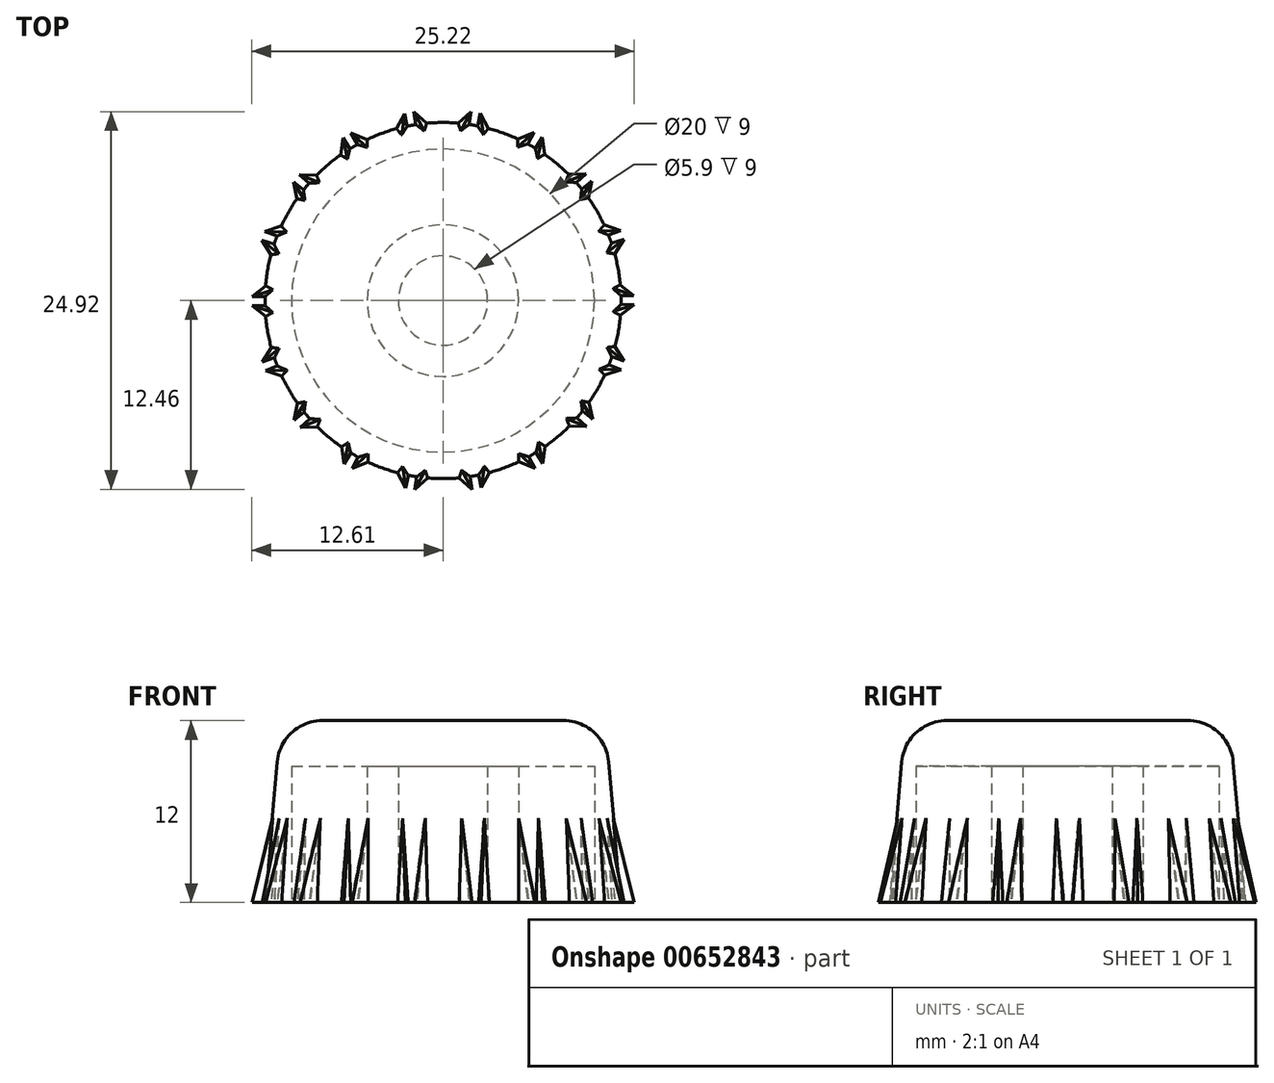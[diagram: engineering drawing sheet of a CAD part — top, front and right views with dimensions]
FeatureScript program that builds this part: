
annotation { "Feature Type Name" : "Feature", "Feature Type Description" : "" }
export const myFeature = defineFeature(function(context is Context, id is Id, definition is map)
    precondition{}
    {
        {
            var Q0;
            Q0=qCreatedBy(makeId("Top.planeOp"),FACE);
            var sketch = newSketch(context, id + "F0", { "sketchPlane" : qUnion([Q0])});
            skLineSegment(sketch, "E0", {"start": v(0, 0) * mm, "end": v(1.85, 12.46) * mm});
            skLineSegment(sketch, "E1", {"start": v(-1.92, 12.46) * mm, "end": v(0, 0) * mm});
            skLineSegment(sketch, "E2", {"start": v(-1.92, 12.46) * mm, "end": v(-0.04, 10.77) * mm});
            skPoint(sketch, "E2.endSnap0", {"position": v(-0.04, 12.46) * mm});
            skLineSegment(sketch, "E3", {"start": v(-0.04, 10.77) * mm, "end": v(1.85, 12.46) * mm});
            skLineSegment(sketch, "E4.1.0", {"start": v(-6.07, 11.05) * mm, "end": v(0, 0) * mm});
            skLineSegment(sketch, "E4.1.1", {"start": v(-3.72, 10.1) * mm, "end": v(-2.53, 12.34) * mm});
            skLineSegment(sketch, "E4.1.2", {"start": v(-6.07, 11.05) * mm, "end": v(-3.72, 10.1) * mm});
            skPoint(sketch, "E4.1.3", {"position": v(-4.3, 11.7) * mm});
            skLineSegment(sketch, "E4.1.4", {"start": v(0, 0) * mm, "end": v(-2.53, 12.34) * mm});
            skLineSegment(sketch, "E4.2.0", {"start": v(-9.48, 8.31) * mm, "end": v(0, 0) * mm});
            skLineSegment(sketch, "E4.2.1", {"start": v(-6.95, 8.23) * mm, "end": v(-6.6, 10.74) * mm});
            skLineSegment(sketch, "E4.2.2", {"start": v(-9.48, 8.31) * mm, "end": v(-6.95, 8.23) * mm});
            skPoint(sketch, "E4.2.3", {"position": v(-8.04, 9.52) * mm});
            skLineSegment(sketch, "E4.2.4", {"start": v(0, 0) * mm, "end": v(-6.6, 10.74) * mm});
            skPoint(sketch, "E4.center", {"position": v(0, 0) * mm});
            skLineSegment(sketch, "E5.1.3.0", {"start": v(-11.75, 4.57) * mm, "end": v(0, 0) * mm});
            skLineSegment(sketch, "E5.3.3.0", {"start": v(-9.35, 5.35) * mm, "end": v(-9.87, 7.83) * mm});
            skLineSegment(sketch, "E5.6.3.0", {"start": v(-11.75, 4.57) * mm, "end": v(-9.35, 5.35) * mm});
            skPoint(sketch, "E5.9.3.0", {"position": v(-10.81, 6.2) * mm});
            skLineSegment(sketch, "E5.10.3.0", {"start": v(0, 0) * mm, "end": v(-9.87, 7.83) * mm});
            skLineSegment(sketch, "E5.1.4.0", {"start": v(-12.6, 0.27) * mm, "end": v(0, 0) * mm});
            skLineSegment(sketch, "E5.3.4.0", {"start": v(-10.61, 1.83) * mm, "end": v(-11.95, 3.98) * mm});
            skLineSegment(sketch, "E5.6.4.0", {"start": v(-12.6, 0.27) * mm, "end": v(-10.61, 1.83) * mm});
            skPoint(sketch, "E5.9.4.0", {"position": v(-12.28, 2.13) * mm});
            skLineSegment(sketch, "E5.10.4.0", {"start": v(0, 0) * mm, "end": v(-11.95, 3.98) * mm});
            skLineSegment(sketch, "E5.1.5.0", {"start": v(-11.94, -4.06) * mm, "end": v(0, 0) * mm});
            skLineSegment(sketch, "E5.3.5.0", {"start": v(-10.6, -1.9) * mm, "end": v(-12.6, -0.35) * mm});
            skLineSegment(sketch, "E5.6.5.0", {"start": v(-11.94, -4.06) * mm, "end": v(-10.6, -1.9) * mm});
            skPoint(sketch, "E5.9.5.0", {"position": v(-12.27, -2.2) * mm});
            skLineSegment(sketch, "E5.10.5.0", {"start": v(0, 0) * mm, "end": v(-12.6, -0.35) * mm});
            skLineSegment(sketch, "E5.1.6.0", {"start": v(-9.83, -7.9) * mm, "end": v(0, 0) * mm});
            skLineSegment(sketch, "E5.3.6.0", {"start": v(-9.3, -5.42) * mm, "end": v(-11.72, -4.63) * mm});
            skLineSegment(sketch, "E5.6.6.0", {"start": v(-9.83, -7.9) * mm, "end": v(-9.3, -5.42) * mm});
            skPoint(sketch, "E5.9.6.0", {"position": v(-10.78, -6.26) * mm});
            skLineSegment(sketch, "E5.10.6.0", {"start": v(0, 0) * mm, "end": v(-11.72, -4.63) * mm});
            skLineSegment(sketch, "E5.1.7.0", {"start": v(-6.54, -10.78) * mm, "end": v(0, 0) * mm});
            skLineSegment(sketch, "E5.3.7.0", {"start": v(-6.9, -8.28) * mm, "end": v(-9.43, -8.36) * mm});
            skLineSegment(sketch, "E5.6.7.0", {"start": v(-6.54, -10.78) * mm, "end": v(-6.9, -8.28) * mm});
            skPoint(sketch, "E5.9.7.0", {"position": v(-7.98, -9.57) * mm});
            skLineSegment(sketch, "E5.10.7.0", {"start": v(0, 0) * mm, "end": v(-9.43, -8.36) * mm});
            skLineSegment(sketch, "E6.1.8.0", {"start": v(-2.46, -12.37) * mm, "end": v(0, 0) * mm});
            skLineSegment(sketch, "E6.3.8.0", {"start": v(-3.65, -10.13) * mm, "end": v(-6, -11.08) * mm});
            skLineSegment(sketch, "E6.6.8.0", {"start": v(-2.46, -12.37) * mm, "end": v(-3.65, -10.13) * mm});
            skPoint(sketch, "E6.9.8.0", {"position": v(-4.23, -11.72) * mm});
            skLineSegment(sketch, "E6.10.8.0", {"start": v(0, 0) * mm, "end": v(-6, -11.08) * mm});
            skLineSegment(sketch, "E6.1.9.0", {"start": v(1.92, -12.46) * mm, "end": v(0, 0) * mm});
            skLineSegment(sketch, "E6.3.9.0", {"start": v(0.04, -10.77) * mm, "end": v(-1.85, -12.46) * mm});
            skLineSegment(sketch, "E6.6.9.0", {"start": v(1.92, -12.46) * mm, "end": v(0.04, -10.77) * mm});
            skPoint(sketch, "E6.9.9.0", {"position": v(0.04, -12.46) * mm});
            skLineSegment(sketch, "E6.10.9.0", {"start": v(0, 0) * mm, "end": v(-1.85, -12.46) * mm});
            skLineSegment(sketch, "E6.1.10.0", {"start": v(6.07, -11.05) * mm, "end": v(0, 0) * mm});
            skLineSegment(sketch, "E6.3.10.0", {"start": v(3.72, -10.1) * mm, "end": v(2.53, -12.34) * mm});
            skLineSegment(sketch, "E6.6.10.0", {"start": v(6.07, -11.05) * mm, "end": v(3.72, -10.1) * mm});
            skPoint(sketch, "E6.9.10.0", {"position": v(4.3, -11.7) * mm});
            skLineSegment(sketch, "E6.10.10.0", {"start": v(0, 0) * mm, "end": v(2.53, -12.34) * mm});
            skLineSegment(sketch, "E6.1.11.0", {"start": v(9.48, -8.31) * mm, "end": v(0, 0) * mm});
            skLineSegment(sketch, "E6.3.11.0", {"start": v(6.95, -8.23) * mm, "end": v(6.6, -10.74) * mm});
            skLineSegment(sketch, "E6.6.11.0", {"start": v(9.48, -8.31) * mm, "end": v(6.95, -8.23) * mm});
            skPoint(sketch, "E6.9.11.0", {"position": v(8.04, -9.52) * mm});
            skLineSegment(sketch, "E6.10.11.0", {"start": v(0, 0) * mm, "end": v(6.6, -10.74) * mm});
            skLineSegment(sketch, "E6.1.12.0", {"start": v(11.75, -4.57) * mm, "end": v(0, 0) * mm});
            skLineSegment(sketch, "E6.3.12.0", {"start": v(9.35, -5.35) * mm, "end": v(9.87, -7.83) * mm});
            skLineSegment(sketch, "E6.6.12.0", {"start": v(11.75, -4.57) * mm, "end": v(9.35, -5.35) * mm});
            skPoint(sketch, "E6.9.12.0", {"position": v(10.81, -6.2) * mm});
            skLineSegment(sketch, "E6.10.12.0", {"start": v(0, 0) * mm, "end": v(9.87, -7.83) * mm});
            skLineSegment(sketch, "E6.1.13.0", {"start": v(12.6, -0.27) * mm, "end": v(0, 0) * mm});
            skLineSegment(sketch, "E6.3.13.0", {"start": v(10.61, -1.83) * mm, "end": v(11.95, -3.98) * mm});
            skLineSegment(sketch, "E6.6.13.0", {"start": v(12.6, -0.27) * mm, "end": v(10.61, -1.83) * mm});
            skPoint(sketch, "E6.9.13.0", {"position": v(12.28, -2.13) * mm});
            skLineSegment(sketch, "E6.10.13.0", {"start": v(0, 0) * mm, "end": v(11.95, -3.98) * mm});
            skLineSegment(sketch, "E6.1.14.0", {"start": v(11.94, 4.06) * mm, "end": v(0, 0) * mm});
            skLineSegment(sketch, "E6.3.14.0", {"start": v(10.6, 1.9) * mm, "end": v(12.6, 0.35) * mm});
            skLineSegment(sketch, "E6.6.14.0", {"start": v(11.94, 4.06) * mm, "end": v(10.6, 1.9) * mm});
            skPoint(sketch, "E6.9.14.0", {"position": v(12.27, 2.2) * mm});
            skLineSegment(sketch, "E6.10.14.0", {"start": v(0, 0) * mm, "end": v(12.6, 0.35) * mm});
            skLineSegment(sketch, "E6.1.15.0", {"start": v(9.83, 7.9) * mm, "end": v(0, 0) * mm});
            skLineSegment(sketch, "E6.3.15.0", {"start": v(9.3, 5.42) * mm, "end": v(11.72, 4.63) * mm});
            skLineSegment(sketch, "E6.6.15.0", {"start": v(9.83, 7.9) * mm, "end": v(9.3, 5.42) * mm});
            skPoint(sketch, "E6.9.15.0", {"position": v(10.78, 6.26) * mm});
            skLineSegment(sketch, "E6.10.15.0", {"start": v(0, 0) * mm, "end": v(11.72, 4.63) * mm});
            skLineSegment(sketch, "E6.1.16.0", {"start": v(6.54, 10.78) * mm, "end": v(0, 0) * mm});
            skLineSegment(sketch, "E6.3.16.0", {"start": v(6.9, 8.28) * mm, "end": v(9.43, 8.36) * mm});
            skLineSegment(sketch, "E6.6.16.0", {"start": v(6.54, 10.78) * mm, "end": v(6.9, 8.28) * mm});
            skPoint(sketch, "E6.9.16.0", {"position": v(7.98, 9.57) * mm});
            skLineSegment(sketch, "E6.10.16.0", {"start": v(0, 0) * mm, "end": v(9.43, 8.36) * mm});
            skLineSegment(sketch, "E6.1.17.0", {"start": v(2.46, 12.37) * mm, "end": v(0, 0) * mm});
            skLineSegment(sketch, "E6.3.17.0", {"start": v(3.65, 10.13) * mm, "end": v(6, 11.08) * mm});
            skLineSegment(sketch, "E6.6.17.0", {"start": v(2.46, 12.37) * mm, "end": v(3.65, 10.13) * mm});
            skPoint(sketch, "E6.9.17.0", {"position": v(4.23, 11.72) * mm});
            skLineSegment(sketch, "E6.10.17.0", {"start": v(0, 0) * mm, "end": v(6, 11.08) * mm});
            skCircle(sketch, "E7", {"center": v(0, 0) * mm, "radius": 10.77 * mm});
            skCircle(sketch, "E8", {"center": v(0, 0) * mm, "radius": 11.75 * mm});
            skSolve(sketch);
        }
        {
            var Q0;
            {var subQ0=sQuery(id+"F0.wireOp",EDGE,"E5.10.6.0");var subQ3=sQuery(id+"F0.wireOp",EDGE,"E7");var subQ5=makeQuery(id+"F0.imprint","INTERSECT",VERTEX,{"derivedFrom":[subQ0,subQ3]});Q0=makeQuery(id+"F0.imprint","IMPRINT",FACE,{"disambiguationData":[TD([[makeQuery(id+"F0.imprint","IMPRINT",EDGE,{"disambiguationData":[TD([[subQ5,-1.0]])],"derivedFrom":subQ3}),1.0]])]});}
            var Q1;
            {var subQ1=sQuery(id+"F0.wireOp",EDGE,"E4.1.1");var subQ3=sQuery(id+"F0.wireOp",EDGE,"E8");var subQ4=makeQuery(id+"F0.imprint","INTERSECT",VERTEX,{"derivedFrom":[subQ1,subQ3]});Q1=makeQuery(id+"F0.imprint","IMPRINT",FACE,{"disambiguationData":[TD([[makeQuery(id+"F0.imprint","IMPRINT",EDGE,{"disambiguationData":[TD([[subQ4,-1.0]])],"derivedFrom":subQ3}),1.0]])]});}
            var Q2;
            {var subQ0=sQuery(id+"F0.wireOp",EDGE,"E8");var subQ1=sQuery(id+"F0.wireOp",EDGE,"E5.1.5.0");var subQ2=makeQuery(id+"F0.imprint","INTERSECT",VERTEX,{"derivedFrom":[subQ1,subQ0]});Q2=makeQuery(id+"F0.imprint","IMPRINT",FACE,{"disambiguationData":[TD([[makeQuery(id+"F0.imprint","IMPRINT",EDGE,{"disambiguationData":[TD([[subQ2,-1.0]])],"derivedFrom":subQ1}),-1.0]])]});}
            var Q3;
            {var subQ0=sQuery(id+"F0.wireOp",EDGE,"E6.10.12.0");var subQ3=sQuery(id+"F0.wireOp",EDGE,"E7");var subQ5=makeQuery(id+"F0.imprint","INTERSECT",VERTEX,{"derivedFrom":[subQ0,subQ3]});Q3=makeQuery(id+"F0.imprint","IMPRINT",FACE,{"disambiguationData":[TD([[makeQuery(id+"F0.imprint","IMPRINT",EDGE,{"disambiguationData":[TD([[subQ5,-1.0]])],"derivedFrom":subQ3}),1.0]])]});}
            var Q4;
            {var subQ3=sQuery(id+"F0.wireOp",EDGE,"E8");var subQ5=sQuery(id+"F0.wireOp",EDGE,"E6.10.17.0");var subQ6=makeQuery(id+"F0.imprint","INTERSECT",VERTEX,{"derivedFrom":[subQ5,subQ3]});Q4=makeQuery(id+"F0.imprint","IMPRINT",FACE,{"disambiguationData":[TD([[makeQuery(id+"F0.imprint","IMPRINT",EDGE,{"disambiguationData":[TD([[subQ6,1.0]])],"derivedFrom":subQ5}),1.0]])]});}
            var Q5;
            {var subQ1=sQuery(id+"F0.wireOp",EDGE,"E5.1.5.0");var subQ3=sQuery(id+"F0.wireOp",EDGE,"E7");var subQ4=makeQuery(id+"F0.imprint","INTERSECT",VERTEX,{"derivedFrom":[subQ1,subQ3]});Q5=makeQuery(id+"F0.imprint","IMPRINT",FACE,{"disambiguationData":[TD([[makeQuery(id+"F0.imprint","IMPRINT",EDGE,{"disambiguationData":[TD([[subQ4,-1.0]])],"derivedFrom":subQ3}),1.0]])]});}
            var Q6;
            {var subQ0=sQuery(id+"F0.wireOp",EDGE,"E8");var subQ1=sQuery(id+"F0.wireOp",EDGE,"E6.1.17.0");var subQ2=makeQuery(id+"F0.imprint","INTERSECT",VERTEX,{"derivedFrom":[subQ1,subQ0]});Q6=makeQuery(id+"F0.imprint","IMPRINT",FACE,{"disambiguationData":[TD([[makeQuery(id+"F0.imprint","IMPRINT",EDGE,{"disambiguationData":[TD([[subQ2,-1.0]])],"derivedFrom":subQ1}),1.0]])]});}
            var Q7;
            {var subQ1=sQuery(id+"F0.wireOp",EDGE,"E1");var subQ3=sQuery(id+"F0.wireOp",EDGE,"E7");var subQ4=makeQuery(id+"F0.imprint","INTERSECT",VERTEX,{"derivedFrom":[subQ1,subQ3]});Q7=makeQuery(id+"F0.imprint","IMPRINT",FACE,{"disambiguationData":[TD([[makeQuery(id+"F0.imprint","IMPRINT",EDGE,{"disambiguationData":[TD([[subQ4,-1.0]])],"derivedFrom":subQ3}),1.0]])]});}
            var Q8;
            {var subQ1=sQuery(id+"F0.wireOp",EDGE,"E0");var subQ3=sQuery(id+"F0.wireOp",EDGE,"E7");var subQ4=makeQuery(id+"F0.imprint","INTERSECT",VERTEX,{"derivedFrom":[subQ1,subQ3]});Q8=makeQuery(id+"F0.imprint","IMPRINT",FACE,{"disambiguationData":[TD([[makeQuery(id+"F0.imprint","IMPRINT",EDGE,{"disambiguationData":[TD([[subQ4,1.0]])],"derivedFrom":subQ3}),1.0]])]});}
            var Q9;
            {var subQ3=sQuery(id+"F0.wireOp",EDGE,"E8");var subQ5=sQuery(id+"F0.wireOp",EDGE,"E6.10.15.0");var subQ6=makeQuery(id+"F0.imprint","INTERSECT",VERTEX,{"derivedFrom":[subQ5,subQ3]});Q9=makeQuery(id+"F0.imprint","IMPRINT",FACE,{"disambiguationData":[TD([[makeQuery(id+"F0.imprint","IMPRINT",EDGE,{"disambiguationData":[TD([[subQ6,1.0]])],"derivedFrom":subQ5}),1.0]])]});}
            var Q10;
            {var subQ0=sQuery(id+"F0.wireOp",EDGE,"E4.2.4");var subQ1=sQuery(id+"F0.wireOp",EDGE,"E4.2.1");var subQ2=makeQuery(id+"F0.imprint","INTERSECT",VERTEX,{"derivedFrom":[subQ1,subQ0]});Q10=makeQuery(id+"F0.imprint","IMPRINT",FACE,{"disambiguationData":[TD([[makeQuery(id+"F0.imprint","IMPRINT",EDGE,{"disambiguationData":[TD([[subQ2,1.0]])],"derivedFrom":subQ1}),-1.0]])]});}
            var Q11;
            {var subQ0=sQuery(id+"F0.wireOp",EDGE,"E8");var subQ1=sQuery(id+"F0.wireOp",EDGE,"E5.1.4.0");var subQ2=makeQuery(id+"F0.imprint","INTERSECT",VERTEX,{"derivedFrom":[subQ1,subQ0]});Q11=makeQuery(id+"F0.imprint","IMPRINT",FACE,{"disambiguationData":[TD([[makeQuery(id+"F0.imprint","IMPRINT",EDGE,{"disambiguationData":[TD([[subQ2,-1.0]])],"derivedFrom":subQ1}),-1.0]])]});}
            var Q12;
            {var subQ0=sQuery(id+"F0.wireOp",EDGE,"E6.6.14.0");var subQ1=sQuery(id+"F0.wireOp",EDGE,"E6.1.14.0");var subQ2=makeQuery(id+"F0.imprint","INTERSECT",VERTEX,{"derivedFrom":[subQ1,subQ0]});Q12=makeQuery(id+"F0.imprint","IMPRINT",FACE,{"disambiguationData":[TD([[makeQuery(id+"F0.imprint","IMPRINT",EDGE,{"disambiguationData":[TD([[subQ2,-1.0]])],"derivedFrom":subQ1}),1.0]])]});}
            var Q13;
            {var subQ1=sQuery(id+"F0.wireOp",EDGE,"E6.1.15.0");var subQ3=sQuery(id+"F0.wireOp",EDGE,"E7");var subQ4=makeQuery(id+"F0.imprint","INTERSECT",VERTEX,{"derivedFrom":[subQ1,subQ3]});Q13=makeQuery(id+"F0.imprint","IMPRINT",FACE,{"disambiguationData":[TD([[makeQuery(id+"F0.imprint","IMPRINT",EDGE,{"disambiguationData":[TD([[subQ4,-1.0]])],"derivedFrom":subQ3}),1.0]])]});}
            var Q14;
            {var subQ0=sQuery(id+"F0.wireOp",EDGE,"E8");var subQ1=sQuery(id+"F0.wireOp",EDGE,"E5.1.7.0");var subQ2=makeQuery(id+"F0.imprint","INTERSECT",VERTEX,{"derivedFrom":[subQ1,subQ0]});Q14=makeQuery(id+"F0.imprint","IMPRINT",FACE,{"disambiguationData":[TD([[makeQuery(id+"F0.imprint","IMPRINT",EDGE,{"disambiguationData":[TD([[subQ2,-1.0]])],"derivedFrom":subQ1}),1.0]])]});}
            var Q15;
            {var subQ3=sQuery(id+"F0.wireOp",EDGE,"E8");var subQ5=sQuery(id+"F0.wireOp",EDGE,"E6.10.13.0");var subQ6=makeQuery(id+"F0.imprint","INTERSECT",VERTEX,{"derivedFrom":[subQ5,subQ3]});Q15=makeQuery(id+"F0.imprint","IMPRINT",FACE,{"disambiguationData":[TD([[makeQuery(id+"F0.imprint","IMPRINT",EDGE,{"disambiguationData":[TD([[subQ6,1.0]])],"derivedFrom":subQ5}),1.0]])]});}
            var Q16;
            {var subQ0=sQuery(id+"F0.wireOp",EDGE,"E4.2.4");var subQ3=sQuery(id+"F0.wireOp",EDGE,"E7");var subQ5=makeQuery(id+"F0.imprint","INTERSECT",VERTEX,{"derivedFrom":[subQ0,subQ3]});Q16=makeQuery(id+"F0.imprint","IMPRINT",FACE,{"disambiguationData":[TD([[makeQuery(id+"F0.imprint","IMPRINT",EDGE,{"disambiguationData":[TD([[subQ5,-1.0]])],"derivedFrom":subQ3}),1.0]])]});}
            var Q17;
            {var subQ1=sQuery(id+"F0.wireOp",EDGE,"E6.3.8.0");var subQ3=sQuery(id+"F0.wireOp",EDGE,"E8");var subQ4=makeQuery(id+"F0.imprint","INTERSECT",VERTEX,{"derivedFrom":[subQ1,subQ3]});Q17=makeQuery(id+"F0.imprint","IMPRINT",FACE,{"disambiguationData":[TD([[makeQuery(id+"F0.imprint","IMPRINT",EDGE,{"disambiguationData":[TD([[subQ4,-1.0]])],"derivedFrom":subQ3}),1.0]])]});}
            var Q18;
            {var subQ0=sQuery(id+"F0.wireOp",EDGE,"E8");var subQ1=sQuery(id+"F0.wireOp",EDGE,"E0");var subQ2=makeQuery(id+"F0.imprint","INTERSECT",VERTEX,{"derivedFrom":[subQ1,subQ0]});Q18=makeQuery(id+"F0.imprint","IMPRINT",FACE,{"disambiguationData":[TD([[makeQuery(id+"F0.imprint","IMPRINT",EDGE,{"disambiguationData":[TD([[subQ2,1.0]])],"derivedFrom":subQ1}),-1.0]])]});}
            var Q19;
            {var subQ0=sQuery(id+"F0.wireOp",EDGE,"E8");var subQ1=sQuery(id+"F0.wireOp",EDGE,"E5.1.6.0");var subQ2=makeQuery(id+"F0.imprint","INTERSECT",VERTEX,{"derivedFrom":[subQ1,subQ0]});Q19=makeQuery(id+"F0.imprint","IMPRINT",FACE,{"disambiguationData":[TD([[makeQuery(id+"F0.imprint","IMPRINT",EDGE,{"disambiguationData":[TD([[subQ2,-1.0]])],"derivedFrom":subQ1}),1.0]])]});}
            var Q20;
            {var subQ0=sQuery(id+"F0.wireOp",EDGE,"E6.6.17.0");var subQ1=sQuery(id+"F0.wireOp",EDGE,"E6.1.17.0");var subQ2=makeQuery(id+"F0.imprint","INTERSECT",VERTEX,{"derivedFrom":[subQ1,subQ0]});Q20=makeQuery(id+"F0.imprint","IMPRINT",FACE,{"disambiguationData":[TD([[makeQuery(id+"F0.imprint","IMPRINT",EDGE,{"disambiguationData":[TD([[subQ2,-1.0]])],"derivedFrom":subQ1}),1.0]])]});}
            var Q21;
            {var subQ0=sQuery(id+"F0.wireOp",EDGE,"E6.10.12.0");var subQ1=sQuery(id+"F0.wireOp",EDGE,"E6.3.12.0");var subQ2=makeQuery(id+"F0.imprint","INTERSECT",VERTEX,{"derivedFrom":[subQ1,subQ0]});Q21=makeQuery(id+"F0.imprint","IMPRINT",FACE,{"disambiguationData":[TD([[makeQuery(id+"F0.imprint","IMPRINT",EDGE,{"disambiguationData":[TD([[subQ2,1.0]])],"derivedFrom":subQ1}),-1.0]])]});}
            var Q22;
            {var subQ0=sQuery(id+"F0.wireOp",EDGE,"E8");var subQ1=sQuery(id+"F0.wireOp",EDGE,"E0");var subQ2=makeQuery(id+"F0.imprint","INTERSECT",VERTEX,{"derivedFrom":[subQ1,subQ0]});Q22=makeQuery(id+"F0.imprint","IMPRINT",FACE,{"disambiguationData":[TD([[makeQuery(id+"F0.imprint","IMPRINT",EDGE,{"disambiguationData":[TD([[subQ2,1.0]])],"derivedFrom":subQ1}),1.0]])]});}
            var Q23;
            {var subQ1=sQuery(id+"F0.wireOp",EDGE,"E5.3.7.0");var subQ3=sQuery(id+"F0.wireOp",EDGE,"E8");var subQ4=makeQuery(id+"F0.imprint","INTERSECT",VERTEX,{"derivedFrom":[subQ1,subQ3]});Q23=makeQuery(id+"F0.imprint","IMPRINT",FACE,{"disambiguationData":[TD([[makeQuery(id+"F0.imprint","IMPRINT",EDGE,{"disambiguationData":[TD([[subQ4,-1.0]])],"derivedFrom":subQ3}),1.0]])]});}
            var Q24;
            {var subQ0=sQuery(id+"F0.wireOp",EDGE,"E6.10.9.0");var subQ3=sQuery(id+"F0.wireOp",EDGE,"E7");var subQ5=makeQuery(id+"F0.imprint","INTERSECT",VERTEX,{"derivedFrom":[subQ0,subQ3]});Q24=makeQuery(id+"F0.imprint","IMPRINT",FACE,{"disambiguationData":[TD([[makeQuery(id+"F0.imprint","IMPRINT",EDGE,{"disambiguationData":[TD([[subQ5,-1.0]])],"derivedFrom":subQ3}),1.0]])]});}
            var Q25;
            {var subQ1=sQuery(id+"F0.wireOp",EDGE,"E5.1.6.0");var subQ3=sQuery(id+"F0.wireOp",EDGE,"E7");var subQ4=makeQuery(id+"F0.imprint","INTERSECT",VERTEX,{"derivedFrom":[subQ1,subQ3]});Q25=makeQuery(id+"F0.imprint","IMPRINT",FACE,{"disambiguationData":[TD([[makeQuery(id+"F0.imprint","IMPRINT",EDGE,{"disambiguationData":[TD([[subQ4,-1.0]])],"derivedFrom":subQ3}),1.0]])]});}
            var Q26;
            {var subQ0=sQuery(id+"F0.wireOp",EDGE,"E6.6.16.0");var subQ1=sQuery(id+"F0.wireOp",EDGE,"E6.1.16.0");var subQ2=makeQuery(id+"F0.imprint","INTERSECT",VERTEX,{"derivedFrom":[subQ1,subQ0]});Q26=makeQuery(id+"F0.imprint","IMPRINT",FACE,{"disambiguationData":[TD([[makeQuery(id+"F0.imprint","IMPRINT",EDGE,{"disambiguationData":[TD([[subQ2,-1.0]])],"derivedFrom":subQ1}),1.0]])]});}
            var Q27;
            {var subQ0=sQuery(id+"F0.wireOp",EDGE,"E5.10.4.0");var subQ3=sQuery(id+"F0.wireOp",EDGE,"E7");var subQ5=makeQuery(id+"F0.imprint","INTERSECT",VERTEX,{"derivedFrom":[subQ0,subQ3]});Q27=makeQuery(id+"F0.imprint","IMPRINT",FACE,{"disambiguationData":[TD([[makeQuery(id+"F0.imprint","IMPRINT",EDGE,{"disambiguationData":[TD([[subQ5,-1.0]])],"derivedFrom":subQ3}),1.0]])]});}
            var Q28;
            {var subQ3=sQuery(id+"F0.wireOp",EDGE,"E8");var subQ5=sQuery(id+"F0.wireOp",EDGE,"E5.10.4.0");var subQ6=makeQuery(id+"F0.imprint","INTERSECT",VERTEX,{"derivedFrom":[subQ5,subQ3]});Q28=makeQuery(id+"F0.imprint","IMPRINT",FACE,{"disambiguationData":[TD([[makeQuery(id+"F0.imprint","IMPRINT",EDGE,{"disambiguationData":[TD([[subQ6,1.0]])],"derivedFrom":subQ5}),1.0]])]});}
            var Q29;
            {var subQ0=sQuery(id+"F0.wireOp",EDGE,"E5.10.3.0");var subQ1=sQuery(id+"F0.wireOp",EDGE,"E5.3.3.0");var subQ2=makeQuery(id+"F0.imprint","INTERSECT",VERTEX,{"derivedFrom":[subQ1,subQ0]});Q29=makeQuery(id+"F0.imprint","IMPRINT",FACE,{"disambiguationData":[TD([[makeQuery(id+"F0.imprint","IMPRINT",EDGE,{"disambiguationData":[TD([[subQ2,1.0]])],"derivedFrom":subQ1}),-1.0]])]});}
            var Q30;
            {var subQ3=sQuery(id+"F0.wireOp",EDGE,"E8");var subQ5=sQuery(id+"F0.wireOp",EDGE,"E6.10.8.0");var subQ6=makeQuery(id+"F0.imprint","INTERSECT",VERTEX,{"derivedFrom":[subQ5,subQ3]});Q30=makeQuery(id+"F0.imprint","IMPRINT",FACE,{"disambiguationData":[TD([[makeQuery(id+"F0.imprint","IMPRINT",EDGE,{"disambiguationData":[TD([[subQ6,1.0]])],"derivedFrom":subQ5}),1.0]])]});}
            var Q31;
            {var subQ0=sQuery(id+"F0.wireOp",EDGE,"E2");var subQ1=sQuery(id+"F0.wireOp",EDGE,"E1");var subQ2=makeQuery(id+"F0.imprint","INTERSECT",VERTEX,{"derivedFrom":[subQ1,subQ0]});Q31=makeQuery(id+"F0.imprint","IMPRINT",FACE,{"disambiguationData":[TD([[makeQuery(id+"F0.imprint","IMPRINT",EDGE,{"disambiguationData":[TD([[subQ2,-1.0]])],"derivedFrom":subQ1}),1.0]])]});}
            var Q32;
            {var subQ1=sQuery(id+"F0.wireOp",EDGE,"E6.1.9.0");var subQ3=sQuery(id+"F0.wireOp",EDGE,"E7");var subQ4=makeQuery(id+"F0.imprint","INTERSECT",VERTEX,{"derivedFrom":[subQ1,subQ3]});Q32=makeQuery(id+"F0.imprint","IMPRINT",FACE,{"disambiguationData":[TD([[makeQuery(id+"F0.imprint","IMPRINT",EDGE,{"disambiguationData":[TD([[subQ4,-1.0]])],"derivedFrom":subQ3}),1.0]])]});}
            var Q33;
            {var subQ0=sQuery(id+"F0.wireOp",EDGE,"E5.10.5.0");var subQ1=sQuery(id+"F0.wireOp",EDGE,"E5.3.5.0");var subQ2=makeQuery(id+"F0.imprint","INTERSECT",VERTEX,{"derivedFrom":[subQ1,subQ0]});Q33=makeQuery(id+"F0.imprint","IMPRINT",FACE,{"disambiguationData":[TD([[makeQuery(id+"F0.imprint","IMPRINT",EDGE,{"disambiguationData":[TD([[subQ2,1.0]])],"derivedFrom":subQ1}),-1.0]])]});}
            var Q34;
            {var subQ3=sQuery(id+"F0.wireOp",EDGE,"E8");var subQ5=sQuery(id+"F0.wireOp",EDGE,"E4.1.4");var subQ6=makeQuery(id+"F0.imprint","INTERSECT",VERTEX,{"derivedFrom":[subQ5,subQ3]});Q34=makeQuery(id+"F0.imprint","IMPRINT",FACE,{"disambiguationData":[TD([[makeQuery(id+"F0.imprint","IMPRINT",EDGE,{"disambiguationData":[TD([[subQ6,1.0]])],"derivedFrom":subQ5}),1.0]])]});}
            var Q35;
            {var subQ3=sQuery(id+"F0.wireOp",EDGE,"E8");var subQ5=sQuery(id+"F0.wireOp",EDGE,"E4.2.4");var subQ6=makeQuery(id+"F0.imprint","INTERSECT",VERTEX,{"derivedFrom":[subQ5,subQ3]});Q35=makeQuery(id+"F0.imprint","IMPRINT",FACE,{"disambiguationData":[TD([[makeQuery(id+"F0.imprint","IMPRINT",EDGE,{"disambiguationData":[TD([[subQ6,1.0]])],"derivedFrom":subQ5}),1.0]])]});}
            var Q36;
            {var subQ0=sQuery(id+"F0.wireOp",EDGE,"E5.6.3.0");var subQ1=sQuery(id+"F0.wireOp",EDGE,"E5.1.3.0");var subQ2=makeQuery(id+"F0.imprint","INTERSECT",VERTEX,{"derivedFrom":[subQ1,subQ0]});Q36=makeQuery(id+"F0.imprint","IMPRINT",FACE,{"disambiguationData":[TD([[makeQuery(id+"F0.imprint","IMPRINT",EDGE,{"disambiguationData":[TD([[subQ2,-1.0]])],"derivedFrom":subQ1}),1.0]])]});}
            var Q37;
            {var subQ0=sQuery(id+"F0.wireOp",EDGE,"E6.6.12.0");var subQ1=sQuery(id+"F0.wireOp",EDGE,"E6.1.12.0");var subQ2=makeQuery(id+"F0.imprint","INTERSECT",VERTEX,{"derivedFrom":[subQ1,subQ0]});Q37=makeQuery(id+"F0.imprint","IMPRINT",FACE,{"disambiguationData":[TD([[makeQuery(id+"F0.imprint","IMPRINT",EDGE,{"disambiguationData":[TD([[subQ2,-1.0]])],"derivedFrom":subQ1}),1.0]])]});}
            var Q38;
            {var subQ0=sQuery(id+"F0.wireOp",EDGE,"E6.10.13.0");var subQ3=sQuery(id+"F0.wireOp",EDGE,"E7");var subQ5=makeQuery(id+"F0.imprint","INTERSECT",VERTEX,{"derivedFrom":[subQ0,subQ3]});Q38=makeQuery(id+"F0.imprint","IMPRINT",FACE,{"disambiguationData":[TD([[makeQuery(id+"F0.imprint","IMPRINT",EDGE,{"disambiguationData":[TD([[subQ5,-1.0]])],"derivedFrom":subQ3}),1.0]])]});}
            var Q39;
            {var subQ0=sQuery(id+"F0.wireOp",EDGE,"E6.6.15.0");var subQ1=sQuery(id+"F0.wireOp",EDGE,"E6.1.15.0");var subQ2=makeQuery(id+"F0.imprint","INTERSECT",VERTEX,{"derivedFrom":[subQ1,subQ0]});Q39=makeQuery(id+"F0.imprint","IMPRINT",FACE,{"disambiguationData":[TD([[makeQuery(id+"F0.imprint","IMPRINT",EDGE,{"disambiguationData":[TD([[subQ2,-1.0]])],"derivedFrom":subQ1}),1.0]])]});}
            var Q40;
            {var subQ0=sQuery(id+"F0.wireOp",EDGE,"E8");var subQ1=sQuery(id+"F0.wireOp",EDGE,"E6.1.8.0");var subQ2=makeQuery(id+"F0.imprint","INTERSECT",VERTEX,{"derivedFrom":[subQ1,subQ0]});Q40=makeQuery(id+"F0.imprint","IMPRINT",FACE,{"disambiguationData":[TD([[makeQuery(id+"F0.imprint","IMPRINT",EDGE,{"disambiguationData":[TD([[subQ2,-1.0]])],"derivedFrom":subQ1}),-1.0]])]});}
            var Q41;
            {var subQ0=sQuery(id+"F0.wireOp",EDGE,"E6.10.14.0");var subQ3=sQuery(id+"F0.wireOp",EDGE,"E7");var subQ5=makeQuery(id+"F0.imprint","INTERSECT",VERTEX,{"derivedFrom":[subQ0,subQ3]});Q41=makeQuery(id+"F0.imprint","IMPRINT",FACE,{"disambiguationData":[TD([[makeQuery(id+"F0.imprint","IMPRINT",EDGE,{"disambiguationData":[TD([[subQ5,-1.0]])],"derivedFrom":subQ3}),1.0]])]});}
            var Q42;
            {var subQ0=sQuery(id+"F0.wireOp",EDGE,"E4.2.2");var subQ1=sQuery(id+"F0.wireOp",EDGE,"E4.2.0");var subQ2=makeQuery(id+"F0.imprint","INTERSECT",VERTEX,{"derivedFrom":[subQ1,subQ0]});Q42=makeQuery(id+"F0.imprint","IMPRINT",FACE,{"disambiguationData":[TD([[makeQuery(id+"F0.imprint","IMPRINT",EDGE,{"disambiguationData":[TD([[subQ2,-1.0]])],"derivedFrom":subQ1}),1.0]])]});}
            var Q43;
            {var subQ0=sQuery(id+"F0.wireOp",EDGE,"E6.10.17.0");var subQ3=sQuery(id+"F0.wireOp",EDGE,"E7");var subQ5=makeQuery(id+"F0.imprint","INTERSECT",VERTEX,{"derivedFrom":[subQ0,subQ3]});Q43=makeQuery(id+"F0.imprint","IMPRINT",FACE,{"disambiguationData":[TD([[makeQuery(id+"F0.imprint","IMPRINT",EDGE,{"disambiguationData":[TD([[subQ5,-1.0]])],"derivedFrom":subQ3}),1.0]])]});}
            var Q44;
            {var subQ1=sQuery(id+"F0.wireOp",EDGE,"E4.1.0");var subQ3=sQuery(id+"F0.wireOp",EDGE,"E7");var subQ4=makeQuery(id+"F0.imprint","INTERSECT",VERTEX,{"derivedFrom":[subQ1,subQ3]});Q44=makeQuery(id+"F0.imprint","IMPRINT",FACE,{"disambiguationData":[TD([[makeQuery(id+"F0.imprint","IMPRINT",EDGE,{"disambiguationData":[TD([[subQ4,-1.0]])],"derivedFrom":subQ3}),1.0]])]});}
            var Q45;
            {var subQ0=sQuery(id+"F0.wireOp",EDGE,"E8");var subQ1=sQuery(id+"F0.wireOp",EDGE,"E6.1.13.0");var subQ2=makeQuery(id+"F0.imprint","INTERSECT",VERTEX,{"derivedFrom":[subQ1,subQ0]});Q45=makeQuery(id+"F0.imprint","IMPRINT",FACE,{"disambiguationData":[TD([[makeQuery(id+"F0.imprint","IMPRINT",EDGE,{"disambiguationData":[TD([[subQ2,-1.0]])],"derivedFrom":subQ1}),1.0]])]});}
            var Q46;
            {var subQ0=sQuery(id+"F0.wireOp",EDGE,"E8");var subQ1=sQuery(id+"F0.wireOp",EDGE,"E6.1.9.0");var subQ2=makeQuery(id+"F0.imprint","INTERSECT",VERTEX,{"derivedFrom":[subQ1,subQ0]});Q46=makeQuery(id+"F0.imprint","IMPRINT",FACE,{"disambiguationData":[TD([[makeQuery(id+"F0.imprint","IMPRINT",EDGE,{"disambiguationData":[TD([[subQ2,-1.0]])],"derivedFrom":subQ1}),1.0]])]});}
            var Q47;
            {var subQ0=sQuery(id+"F0.wireOp",EDGE,"E8");var subQ1=sQuery(id+"F0.wireOp",EDGE,"E6.1.15.0");var subQ2=makeQuery(id+"F0.imprint","INTERSECT",VERTEX,{"derivedFrom":[subQ1,subQ0]});Q47=makeQuery(id+"F0.imprint","IMPRINT",FACE,{"disambiguationData":[TD([[makeQuery(id+"F0.imprint","IMPRINT",EDGE,{"disambiguationData":[TD([[subQ2,-1.0]])],"derivedFrom":subQ1}),1.0]])]});}
            var Q48;
            {var subQ0=sQuery(id+"F0.wireOp",EDGE,"E8");var subQ1=sQuery(id+"F0.wireOp",EDGE,"E6.1.12.0");var subQ2=makeQuery(id+"F0.imprint","INTERSECT",VERTEX,{"derivedFrom":[subQ1,subQ0]});Q48=makeQuery(id+"F0.imprint","IMPRINT",FACE,{"disambiguationData":[TD([[makeQuery(id+"F0.imprint","IMPRINT",EDGE,{"disambiguationData":[TD([[subQ2,-1.0]])],"derivedFrom":subQ1}),1.0]])]});}
            var Q49;
            {var subQ1=sQuery(id+"F0.wireOp",EDGE,"E6.3.14.0");var subQ3=sQuery(id+"F0.wireOp",EDGE,"E8");var subQ4=makeQuery(id+"F0.imprint","INTERSECT",VERTEX,{"derivedFrom":[subQ1,subQ3]});Q49=makeQuery(id+"F0.imprint","IMPRINT",FACE,{"disambiguationData":[TD([[makeQuery(id+"F0.imprint","IMPRINT",EDGE,{"disambiguationData":[TD([[subQ4,-1.0]])],"derivedFrom":subQ3}),1.0]])]});}
            var Q50;
            {var subQ1=sQuery(id+"F0.wireOp",EDGE,"E6.1.13.0");var subQ3=sQuery(id+"F0.wireOp",EDGE,"E7");var subQ4=makeQuery(id+"F0.imprint","INTERSECT",VERTEX,{"derivedFrom":[subQ1,subQ3]});Q50=makeQuery(id+"F0.imprint","IMPRINT",FACE,{"disambiguationData":[TD([[makeQuery(id+"F0.imprint","IMPRINT",EDGE,{"disambiguationData":[TD([[subQ4,-1.0]])],"derivedFrom":subQ3}),1.0]])]});}
            var Q51;
            {var subQ0=sQuery(id+"F0.wireOp",EDGE,"E3");var subQ1=sQuery(id+"F0.wireOp",EDGE,"E0");var subQ2=makeQuery(id+"F0.imprint","INTERSECT",VERTEX,{"derivedFrom":[subQ1,subQ0]});Q51=makeQuery(id+"F0.imprint","IMPRINT",FACE,{"disambiguationData":[TD([[makeQuery(id+"F0.imprint","IMPRINT",EDGE,{"disambiguationData":[TD([[subQ2,1.0]])],"derivedFrom":subQ1}),1.0]])]});}
            var Q52;
            Q52 = qSketchRegion(id + "F0", true);
            var Q53;
            {var subQ0=sQuery(id+"F0.wireOp",EDGE,"E8");var subQ1=sQuery(id+"F0.wireOp",EDGE,"E5.1.6.0");var subQ2=makeQuery(id+"F0.imprint","INTERSECT",VERTEX,{"derivedFrom":[subQ1,subQ0]});Q53=makeQuery(id+"F0.imprint","IMPRINT",FACE,{"disambiguationData":[TD([[makeQuery(id+"F0.imprint","IMPRINT",EDGE,{"disambiguationData":[TD([[subQ2,-1.0]])],"derivedFrom":subQ1}),-1.0]])]});}
            var Q54;
            {var subQ0=sQuery(id+"F0.wireOp",EDGE,"E6.10.8.0");var subQ1=sQuery(id+"F0.wireOp",EDGE,"E6.3.8.0");var subQ2=makeQuery(id+"F0.imprint","INTERSECT",VERTEX,{"derivedFrom":[subQ1,subQ0]});Q54=makeQuery(id+"F0.imprint","IMPRINT",FACE,{"disambiguationData":[TD([[makeQuery(id+"F0.imprint","IMPRINT",EDGE,{"disambiguationData":[TD([[subQ2,1.0]])],"derivedFrom":subQ1}),-1.0]])]});}
            var Q55;
            {var subQ0=sQuery(id+"F0.wireOp",EDGE,"E6.10.8.0");var subQ3=sQuery(id+"F0.wireOp",EDGE,"E7");var subQ5=makeQuery(id+"F0.imprint","INTERSECT",VERTEX,{"derivedFrom":[subQ0,subQ3]});Q55=makeQuery(id+"F0.imprint","IMPRINT",FACE,{"disambiguationData":[TD([[makeQuery(id+"F0.imprint","IMPRINT",EDGE,{"disambiguationData":[TD([[subQ5,-1.0]])],"derivedFrom":subQ3}),1.0]])]});}
            var Q56;
            {var subQ0=sQuery(id+"F0.wireOp",EDGE,"E4.1.4");var subQ3=sQuery(id+"F0.wireOp",EDGE,"E7");var subQ5=makeQuery(id+"F0.imprint","INTERSECT",VERTEX,{"derivedFrom":[subQ0,subQ3]});Q56=makeQuery(id+"F0.imprint","IMPRINT",FACE,{"disambiguationData":[TD([[makeQuery(id+"F0.imprint","IMPRINT",EDGE,{"disambiguationData":[TD([[subQ5,-1.0]])],"derivedFrom":subQ3}),1.0]])]});}
            var Q57;
            {var subQ0=sQuery(id+"F0.wireOp",EDGE,"E8");var subQ1=sQuery(id+"F0.wireOp",EDGE,"E6.1.12.0");var subQ2=makeQuery(id+"F0.imprint","INTERSECT",VERTEX,{"derivedFrom":[subQ1,subQ0]});Q57=makeQuery(id+"F0.imprint","IMPRINT",FACE,{"disambiguationData":[TD([[makeQuery(id+"F0.imprint","IMPRINT",EDGE,{"disambiguationData":[TD([[subQ2,-1.0]])],"derivedFrom":subQ1}),-1.0]])]});}
            var Q58;
            {var subQ0=sQuery(id+"F0.wireOp",EDGE,"E5.6.5.0");var subQ1=sQuery(id+"F0.wireOp",EDGE,"E5.1.5.0");var subQ2=makeQuery(id+"F0.imprint","INTERSECT",VERTEX,{"derivedFrom":[subQ1,subQ0]});Q58=makeQuery(id+"F0.imprint","IMPRINT",FACE,{"disambiguationData":[TD([[makeQuery(id+"F0.imprint","IMPRINT",EDGE,{"disambiguationData":[TD([[subQ2,-1.0]])],"derivedFrom":subQ1}),1.0]])]});}
            var Q59;
            {var subQ0=sQuery(id+"F0.wireOp",EDGE,"E5.6.4.0");var subQ1=sQuery(id+"F0.wireOp",EDGE,"E5.1.4.0");var subQ2=makeQuery(id+"F0.imprint","INTERSECT",VERTEX,{"derivedFrom":[subQ1,subQ0]});Q59=makeQuery(id+"F0.imprint","IMPRINT",FACE,{"disambiguationData":[TD([[makeQuery(id+"F0.imprint","IMPRINT",EDGE,{"disambiguationData":[TD([[subQ2,-1.0]])],"derivedFrom":subQ1}),1.0]])]});}
            var Q60;
            {var subQ3=sQuery(id+"F0.wireOp",EDGE,"E8");var subQ5=sQuery(id+"F0.wireOp",EDGE,"E6.10.11.0");var subQ6=makeQuery(id+"F0.imprint","INTERSECT",VERTEX,{"derivedFrom":[subQ5,subQ3]});Q60=makeQuery(id+"F0.imprint","IMPRINT",FACE,{"disambiguationData":[TD([[makeQuery(id+"F0.imprint","IMPRINT",EDGE,{"disambiguationData":[TD([[subQ6,1.0]])],"derivedFrom":subQ5}),1.0]])]});}
            var Q61;
            {var subQ3=sQuery(id+"F0.wireOp",EDGE,"E8");var subQ5=sQuery(id+"F0.wireOp",EDGE,"E6.10.14.0");var subQ6=makeQuery(id+"F0.imprint","INTERSECT",VERTEX,{"derivedFrom":[subQ5,subQ3]});Q61=makeQuery(id+"F0.imprint","IMPRINT",FACE,{"disambiguationData":[TD([[makeQuery(id+"F0.imprint","IMPRINT",EDGE,{"disambiguationData":[TD([[subQ6,1.0]])],"derivedFrom":subQ5}),1.0]])]});}
            var Q62;
            {var subQ0=sQuery(id+"F0.wireOp",EDGE,"E8");var subQ1=sQuery(id+"F0.wireOp",EDGE,"E6.1.14.0");var subQ2=makeQuery(id+"F0.imprint","INTERSECT",VERTEX,{"derivedFrom":[subQ1,subQ0]});Q62=makeQuery(id+"F0.imprint","IMPRINT",FACE,{"disambiguationData":[TD([[makeQuery(id+"F0.imprint","IMPRINT",EDGE,{"disambiguationData":[TD([[subQ2,-1.0]])],"derivedFrom":subQ1}),-1.0]])]});}
            var Q63;
            {var subQ3=sQuery(id+"F0.wireOp",EDGE,"E8");var subQ5=sQuery(id+"F0.wireOp",EDGE,"E5.10.3.0");var subQ6=makeQuery(id+"F0.imprint","INTERSECT",VERTEX,{"derivedFrom":[subQ5,subQ3]});Q63=makeQuery(id+"F0.imprint","IMPRINT",FACE,{"disambiguationData":[TD([[makeQuery(id+"F0.imprint","IMPRINT",EDGE,{"disambiguationData":[TD([[subQ6,1.0]])],"derivedFrom":subQ5}),1.0]])]});}
            var Q64;
            {var subQ3=sQuery(id+"F0.wireOp",EDGE,"E8");var subQ5=sQuery(id+"F0.wireOp",EDGE,"E6.10.10.0");var subQ6=makeQuery(id+"F0.imprint","INTERSECT",VERTEX,{"derivedFrom":[subQ5,subQ3]});Q64=makeQuery(id+"F0.imprint","IMPRINT",FACE,{"disambiguationData":[TD([[makeQuery(id+"F0.imprint","IMPRINT",EDGE,{"disambiguationData":[TD([[subQ6,1.0]])],"derivedFrom":subQ5}),1.0]])]});}
            var Q65;
            {var subQ0=sQuery(id+"F0.wireOp",EDGE,"E8");var subQ1=sQuery(id+"F0.wireOp",EDGE,"E5.1.4.0");var subQ2=makeQuery(id+"F0.imprint","INTERSECT",VERTEX,{"derivedFrom":[subQ1,subQ0]});Q65=makeQuery(id+"F0.imprint","IMPRINT",FACE,{"disambiguationData":[TD([[makeQuery(id+"F0.imprint","IMPRINT",EDGE,{"disambiguationData":[TD([[subQ2,-1.0]])],"derivedFrom":subQ1}),1.0]])]});}
            var Q66;
            {var subQ1=sQuery(id+"F0.wireOp",EDGE,"E6.3.12.0");var subQ3=sQuery(id+"F0.wireOp",EDGE,"E8");var subQ4=makeQuery(id+"F0.imprint","INTERSECT",VERTEX,{"derivedFrom":[subQ1,subQ3]});Q66=makeQuery(id+"F0.imprint","IMPRINT",FACE,{"disambiguationData":[TD([[makeQuery(id+"F0.imprint","IMPRINT",EDGE,{"disambiguationData":[TD([[subQ4,-1.0]])],"derivedFrom":subQ3}),1.0]])]});}
            var Q67;
            {var subQ0=sQuery(id+"F0.wireOp",EDGE,"E8");var subQ1=sQuery(id+"F0.wireOp",EDGE,"E5.1.5.0");var subQ2=makeQuery(id+"F0.imprint","INTERSECT",VERTEX,{"derivedFrom":[subQ1,subQ0]});Q67=makeQuery(id+"F0.imprint","IMPRINT",FACE,{"disambiguationData":[TD([[makeQuery(id+"F0.imprint","IMPRINT",EDGE,{"disambiguationData":[TD([[subQ2,-1.0]])],"derivedFrom":subQ1}),1.0]])]});}
            var Q68;
            {var subQ1=sQuery(id+"F0.wireOp",EDGE,"E4.2.0");var subQ3=sQuery(id+"F0.wireOp",EDGE,"E7");var subQ4=makeQuery(id+"F0.imprint","INTERSECT",VERTEX,{"derivedFrom":[subQ1,subQ3]});Q68=makeQuery(id+"F0.imprint","IMPRINT",FACE,{"disambiguationData":[TD([[makeQuery(id+"F0.imprint","IMPRINT",EDGE,{"disambiguationData":[TD([[subQ4,-1.0]])],"derivedFrom":subQ3}),1.0]])]});}
            var Q69;
            {var subQ3=sQuery(id+"F0.wireOp",EDGE,"E8");var subQ5=sQuery(id+"F0.wireOp",EDGE,"E6.10.12.0");var subQ6=makeQuery(id+"F0.imprint","INTERSECT",VERTEX,{"derivedFrom":[subQ5,subQ3]});Q69=makeQuery(id+"F0.imprint","IMPRINT",FACE,{"disambiguationData":[TD([[makeQuery(id+"F0.imprint","IMPRINT",EDGE,{"disambiguationData":[TD([[subQ6,1.0]])],"derivedFrom":subQ5}),1.0]])]});}
            var Q70;
            {var subQ1=sQuery(id+"F0.wireOp",EDGE,"E4.2.1");var subQ3=sQuery(id+"F0.wireOp",EDGE,"E8");var subQ4=makeQuery(id+"F0.imprint","INTERSECT",VERTEX,{"derivedFrom":[subQ1,subQ3]});Q70=makeQuery(id+"F0.imprint","IMPRINT",FACE,{"disambiguationData":[TD([[makeQuery(id+"F0.imprint","IMPRINT",EDGE,{"disambiguationData":[TD([[subQ4,-1.0]])],"derivedFrom":subQ3}),1.0]])]});}
            var Q71;
            {var subQ0=sQuery(id+"F0.wireOp",EDGE,"E8");var subQ1=sQuery(id+"F0.wireOp",EDGE,"E4.2.0");var subQ2=makeQuery(id+"F0.imprint","INTERSECT",VERTEX,{"derivedFrom":[subQ1,subQ0]});Q71=makeQuery(id+"F0.imprint","IMPRINT",FACE,{"disambiguationData":[TD([[makeQuery(id+"F0.imprint","IMPRINT",EDGE,{"disambiguationData":[TD([[subQ2,-1.0]])],"derivedFrom":subQ1}),1.0]])]});}
            var Q72;
            {var subQ0=sQuery(id+"F0.wireOp",EDGE,"E8");var subQ1=sQuery(id+"F0.wireOp",EDGE,"E6.1.16.0");var subQ2=makeQuery(id+"F0.imprint","INTERSECT",VERTEX,{"derivedFrom":[subQ1,subQ0]});Q72=makeQuery(id+"F0.imprint","IMPRINT",FACE,{"disambiguationData":[TD([[makeQuery(id+"F0.imprint","IMPRINT",EDGE,{"disambiguationData":[TD([[subQ2,-1.0]])],"derivedFrom":subQ1}),-1.0]])]});}
            var Q73;
            {var subQ0=sQuery(id+"F0.wireOp",EDGE,"E8");var subQ1=sQuery(id+"F0.wireOp",EDGE,"E5.1.3.0");var subQ2=makeQuery(id+"F0.imprint","INTERSECT",VERTEX,{"derivedFrom":[subQ1,subQ0]});Q73=makeQuery(id+"F0.imprint","IMPRINT",FACE,{"disambiguationData":[TD([[makeQuery(id+"F0.imprint","IMPRINT",EDGE,{"disambiguationData":[TD([[subQ2,-1.0]])],"derivedFrom":subQ1}),-1.0]])]});}
            var Q74;
            {var subQ1=sQuery(id+"F0.wireOp",EDGE,"E5.1.7.0");var subQ3=sQuery(id+"F0.wireOp",EDGE,"E7");var subQ4=makeQuery(id+"F0.imprint","INTERSECT",VERTEX,{"derivedFrom":[subQ1,subQ3]});Q74=makeQuery(id+"F0.imprint","IMPRINT",FACE,{"disambiguationData":[TD([[makeQuery(id+"F0.imprint","IMPRINT",EDGE,{"disambiguationData":[TD([[subQ4,-1.0]])],"derivedFrom":subQ3}),1.0]])]});}
            var Q75;
            {var subQ1=sQuery(id+"F0.wireOp",EDGE,"E6.1.11.0");var subQ3=sQuery(id+"F0.wireOp",EDGE,"E7");var subQ4=makeQuery(id+"F0.imprint","INTERSECT",VERTEX,{"derivedFrom":[subQ1,subQ3]});Q75=makeQuery(id+"F0.imprint","IMPRINT",FACE,{"disambiguationData":[TD([[makeQuery(id+"F0.imprint","IMPRINT",EDGE,{"disambiguationData":[TD([[subQ4,-1.0]])],"derivedFrom":subQ3}),1.0]])]});}
            var Q76;
            {var subQ0=sQuery(id+"F0.wireOp",EDGE,"E8");var subQ1=sQuery(id+"F0.wireOp",EDGE,"E6.1.15.0");var subQ2=makeQuery(id+"F0.imprint","INTERSECT",VERTEX,{"derivedFrom":[subQ1,subQ0]});Q76=makeQuery(id+"F0.imprint","IMPRINT",FACE,{"disambiguationData":[TD([[makeQuery(id+"F0.imprint","IMPRINT",EDGE,{"disambiguationData":[TD([[subQ2,-1.0]])],"derivedFrom":subQ1}),-1.0]])]});}
            var Q77;
            {var subQ0=sQuery(id+"F0.wireOp",EDGE,"E5.6.6.0");var subQ1=sQuery(id+"F0.wireOp",EDGE,"E5.1.6.0");var subQ2=makeQuery(id+"F0.imprint","INTERSECT",VERTEX,{"derivedFrom":[subQ1,subQ0]});Q77=makeQuery(id+"F0.imprint","IMPRINT",FACE,{"disambiguationData":[TD([[makeQuery(id+"F0.imprint","IMPRINT",EDGE,{"disambiguationData":[TD([[subQ2,-1.0]])],"derivedFrom":subQ1}),1.0]])]});}
            var Q78;
            {var subQ1=sQuery(id+"F0.wireOp",EDGE,"E6.3.16.0");var subQ3=sQuery(id+"F0.wireOp",EDGE,"E8");var subQ4=makeQuery(id+"F0.imprint","INTERSECT",VERTEX,{"derivedFrom":[subQ1,subQ3]});Q78=makeQuery(id+"F0.imprint","IMPRINT",FACE,{"disambiguationData":[TD([[makeQuery(id+"F0.imprint","IMPRINT",EDGE,{"disambiguationData":[TD([[subQ4,-1.0]])],"derivedFrom":subQ3}),1.0]])]});}
            var Q79;
            {var subQ1=sQuery(id+"F0.wireOp",EDGE,"E6.1.8.0");var subQ3=sQuery(id+"F0.wireOp",EDGE,"E7");var subQ4=makeQuery(id+"F0.imprint","INTERSECT",VERTEX,{"derivedFrom":[subQ1,subQ3]});Q79=makeQuery(id+"F0.imprint","IMPRINT",FACE,{"disambiguationData":[TD([[makeQuery(id+"F0.imprint","IMPRINT",EDGE,{"disambiguationData":[TD([[subQ4,-1.0]])],"derivedFrom":subQ3}),1.0]])]});}
            var Q80;
            {var subQ0=sQuery(id+"F0.wireOp",EDGE,"E8");var subQ1=sQuery(id+"F0.wireOp",EDGE,"E4.1.0");var subQ2=makeQuery(id+"F0.imprint","INTERSECT",VERTEX,{"derivedFrom":[subQ1,subQ0]});Q80=makeQuery(id+"F0.imprint","IMPRINT",FACE,{"disambiguationData":[TD([[makeQuery(id+"F0.imprint","IMPRINT",EDGE,{"disambiguationData":[TD([[subQ2,-1.0]])],"derivedFrom":subQ1}),1.0]])]});}
            var Q81;
            {var subQ0=sQuery(id+"F0.wireOp",EDGE,"E5.6.7.0");var subQ1=sQuery(id+"F0.wireOp",EDGE,"E5.1.7.0");var subQ2=makeQuery(id+"F0.imprint","INTERSECT",VERTEX,{"derivedFrom":[subQ1,subQ0]});Q81=makeQuery(id+"F0.imprint","IMPRINT",FACE,{"disambiguationData":[TD([[makeQuery(id+"F0.imprint","IMPRINT",EDGE,{"disambiguationData":[TD([[subQ2,-1.0]])],"derivedFrom":subQ1}),1.0]])]});}
            var Q82;
            {var subQ3=sQuery(id+"F0.wireOp",EDGE,"E8");var subQ5=sQuery(id+"F0.wireOp",EDGE,"E5.10.5.0");var subQ6=makeQuery(id+"F0.imprint","INTERSECT",VERTEX,{"derivedFrom":[subQ5,subQ3]});Q82=makeQuery(id+"F0.imprint","IMPRINT",FACE,{"disambiguationData":[TD([[makeQuery(id+"F0.imprint","IMPRINT",EDGE,{"disambiguationData":[TD([[subQ6,1.0]])],"derivedFrom":subQ5}),1.0]])]});}
            var Q83;
            {var subQ0=sQuery(id+"F0.wireOp",EDGE,"E8");var subQ1=sQuery(id+"F0.wireOp",EDGE,"E1");var subQ2=makeQuery(id+"F0.imprint","INTERSECT",VERTEX,{"derivedFrom":[subQ1,subQ0]});Q83=makeQuery(id+"F0.imprint","IMPRINT",FACE,{"disambiguationData":[TD([[makeQuery(id+"F0.imprint","IMPRINT",EDGE,{"disambiguationData":[TD([[subQ2,-1.0]])],"derivedFrom":subQ1}),1.0]])]});}
            var Q84;
            {var subQ0=sQuery(id+"F0.wireOp",EDGE,"E5.10.3.0");var subQ3=sQuery(id+"F0.wireOp",EDGE,"E7");var subQ5=makeQuery(id+"F0.imprint","INTERSECT",VERTEX,{"derivedFrom":[subQ0,subQ3]});Q84=makeQuery(id+"F0.imprint","IMPRINT",FACE,{"disambiguationData":[TD([[makeQuery(id+"F0.imprint","IMPRINT",EDGE,{"disambiguationData":[TD([[subQ5,-1.0]])],"derivedFrom":subQ3}),1.0]])]});}
            var Q85;
            {var subQ0=sQuery(id+"F0.wireOp",EDGE,"E4.1.2");var subQ1=sQuery(id+"F0.wireOp",EDGE,"E4.1.0");var subQ2=makeQuery(id+"F0.imprint","INTERSECT",VERTEX,{"derivedFrom":[subQ1,subQ0]});Q85=makeQuery(id+"F0.imprint","IMPRINT",FACE,{"disambiguationData":[TD([[makeQuery(id+"F0.imprint","IMPRINT",EDGE,{"disambiguationData":[TD([[subQ2,-1.0]])],"derivedFrom":subQ1}),1.0]])]});}
            var Q86;
            {var subQ0=sQuery(id+"F0.wireOp",EDGE,"E5.10.6.0");var subQ1=sQuery(id+"F0.wireOp",EDGE,"E5.3.6.0");var subQ2=makeQuery(id+"F0.imprint","INTERSECT",VERTEX,{"derivedFrom":[subQ1,subQ0]});Q86=makeQuery(id+"F0.imprint","IMPRINT",FACE,{"disambiguationData":[TD([[makeQuery(id+"F0.imprint","IMPRINT",EDGE,{"disambiguationData":[TD([[subQ2,1.0]])],"derivedFrom":subQ1}),-1.0]])]});}
            var Q87;
            {var subQ1=sQuery(id+"F0.wireOp",EDGE,"E6.3.11.0");var subQ3=sQuery(id+"F0.wireOp",EDGE,"E8");var subQ4=makeQuery(id+"F0.imprint","INTERSECT",VERTEX,{"derivedFrom":[subQ1,subQ3]});Q87=makeQuery(id+"F0.imprint","IMPRINT",FACE,{"disambiguationData":[TD([[makeQuery(id+"F0.imprint","IMPRINT",EDGE,{"disambiguationData":[TD([[subQ4,-1.0]])],"derivedFrom":subQ3}),1.0]])]});}
            var Q88;
            {var subQ1=sQuery(id+"F0.wireOp",EDGE,"E6.3.9.0");var subQ3=sQuery(id+"F0.wireOp",EDGE,"E8");var subQ4=makeQuery(id+"F0.imprint","INTERSECT",VERTEX,{"derivedFrom":[subQ1,subQ3]});Q88=makeQuery(id+"F0.imprint","IMPRINT",FACE,{"disambiguationData":[TD([[makeQuery(id+"F0.imprint","IMPRINT",EDGE,{"disambiguationData":[TD([[subQ4,-1.0]])],"derivedFrom":subQ3}),1.0]])]});}
            var Q89;
            {var subQ1=sQuery(id+"F0.wireOp",EDGE,"E6.1.16.0");var subQ3=sQuery(id+"F0.wireOp",EDGE,"E7");var subQ4=makeQuery(id+"F0.imprint","INTERSECT",VERTEX,{"derivedFrom":[subQ1,subQ3]});Q89=makeQuery(id+"F0.imprint","IMPRINT",FACE,{"disambiguationData":[TD([[makeQuery(id+"F0.imprint","IMPRINT",EDGE,{"disambiguationData":[TD([[subQ4,-1.0]])],"derivedFrom":subQ3}),1.0]])]});}
            var Q90;
            {var subQ0=sQuery(id+"F0.wireOp",EDGE,"E6.10.16.0");var subQ1=sQuery(id+"F0.wireOp",EDGE,"E6.3.16.0");var subQ2=makeQuery(id+"F0.imprint","INTERSECT",VERTEX,{"derivedFrom":[subQ1,subQ0]});Q90=makeQuery(id+"F0.imprint","IMPRINT",FACE,{"disambiguationData":[TD([[makeQuery(id+"F0.imprint","IMPRINT",EDGE,{"disambiguationData":[TD([[subQ2,1.0]])],"derivedFrom":subQ1}),-1.0]])]});}
            var Q91;
            {var subQ1=sQuery(id+"F0.wireOp",EDGE,"E5.1.3.0");var subQ3=sQuery(id+"F0.wireOp",EDGE,"E7");var subQ4=makeQuery(id+"F0.imprint","INTERSECT",VERTEX,{"derivedFrom":[subQ1,subQ3]});Q91=makeQuery(id+"F0.imprint","IMPRINT",FACE,{"disambiguationData":[TD([[makeQuery(id+"F0.imprint","IMPRINT",EDGE,{"disambiguationData":[TD([[subQ4,-1.0]])],"derivedFrom":subQ3}),1.0]])]});}
            var Q92;
            {var subQ0=sQuery(id+"F0.wireOp",EDGE,"E5.10.7.0");var subQ1=sQuery(id+"F0.wireOp",EDGE,"E5.3.7.0");var subQ2=makeQuery(id+"F0.imprint","INTERSECT",VERTEX,{"derivedFrom":[subQ1,subQ0]});Q92=makeQuery(id+"F0.imprint","IMPRINT",FACE,{"disambiguationData":[TD([[makeQuery(id+"F0.imprint","IMPRINT",EDGE,{"disambiguationData":[TD([[subQ2,1.0]])],"derivedFrom":subQ1}),-1.0]])]});}
            var Q93;
            {var subQ0=sQuery(id+"F0.wireOp",EDGE,"E6.10.11.0");var subQ3=sQuery(id+"F0.wireOp",EDGE,"E7");var subQ5=makeQuery(id+"F0.imprint","INTERSECT",VERTEX,{"derivedFrom":[subQ0,subQ3]});Q93=makeQuery(id+"F0.imprint","IMPRINT",FACE,{"disambiguationData":[TD([[makeQuery(id+"F0.imprint","IMPRINT",EDGE,{"disambiguationData":[TD([[subQ5,-1.0]])],"derivedFrom":subQ3}),1.0]])]});}
            var Q94;
            {var subQ1=sQuery(id+"F0.wireOp",EDGE,"E2");var subQ3=sQuery(id+"F0.wireOp",EDGE,"E8");var subQ4=makeQuery(id+"F0.imprint","INTERSECT",VERTEX,{"derivedFrom":[subQ1,subQ3]});Q94=makeQuery(id+"F0.imprint","IMPRINT",FACE,{"disambiguationData":[TD([[makeQuery(id+"F0.imprint","IMPRINT",EDGE,{"disambiguationData":[TD([[subQ4,1.0]])],"derivedFrom":subQ3}),1.0]])]});}
            var Q95;
            {var subQ0=sQuery(id+"F0.wireOp",EDGE,"E8");var subQ1=sQuery(id+"F0.wireOp",EDGE,"E6.1.10.0");var subQ2=makeQuery(id+"F0.imprint","INTERSECT",VERTEX,{"derivedFrom":[subQ1,subQ0]});Q95=makeQuery(id+"F0.imprint","IMPRINT",FACE,{"disambiguationData":[TD([[makeQuery(id+"F0.imprint","IMPRINT",EDGE,{"disambiguationData":[TD([[subQ2,-1.0]])],"derivedFrom":subQ1}),1.0]])]});}
            var Q96;
            {var subQ1=sQuery(id+"F0.wireOp",EDGE,"E6.3.13.0");var subQ3=sQuery(id+"F0.wireOp",EDGE,"E8");var subQ4=makeQuery(id+"F0.imprint","INTERSECT",VERTEX,{"derivedFrom":[subQ1,subQ3]});Q96=makeQuery(id+"F0.imprint","IMPRINT",FACE,{"disambiguationData":[TD([[makeQuery(id+"F0.imprint","IMPRINT",EDGE,{"disambiguationData":[TD([[subQ4,-1.0]])],"derivedFrom":subQ3}),1.0]])]});}
            var Q97;
            {var subQ1=sQuery(id+"F0.wireOp",EDGE,"E5.3.6.0");var subQ3=sQuery(id+"F0.wireOp",EDGE,"E8");var subQ4=makeQuery(id+"F0.imprint","INTERSECT",VERTEX,{"derivedFrom":[subQ1,subQ3]});Q97=makeQuery(id+"F0.imprint","IMPRINT",FACE,{"disambiguationData":[TD([[makeQuery(id+"F0.imprint","IMPRINT",EDGE,{"disambiguationData":[TD([[subQ4,-1.0]])],"derivedFrom":subQ3}),1.0]])]});}
            var Q98;
            {var subQ0=sQuery(id+"F0.wireOp",EDGE,"E8");var subQ1=sQuery(id+"F0.wireOp",EDGE,"E6.1.14.0");var subQ2=makeQuery(id+"F0.imprint","INTERSECT",VERTEX,{"derivedFrom":[subQ1,subQ0]});Q98=makeQuery(id+"F0.imprint","IMPRINT",FACE,{"disambiguationData":[TD([[makeQuery(id+"F0.imprint","IMPRINT",EDGE,{"disambiguationData":[TD([[subQ2,-1.0]])],"derivedFrom":subQ1}),1.0]])]});}
            var Q99;
            {var subQ0=sQuery(id+"F0.wireOp",EDGE,"E8");var subQ1=sQuery(id+"F0.wireOp",EDGE,"E4.1.0");var subQ2=makeQuery(id+"F0.imprint","INTERSECT",VERTEX,{"derivedFrom":[subQ1,subQ0]});Q99=makeQuery(id+"F0.imprint","IMPRINT",FACE,{"disambiguationData":[TD([[makeQuery(id+"F0.imprint","IMPRINT",EDGE,{"disambiguationData":[TD([[subQ2,-1.0]])],"derivedFrom":subQ1}),-1.0]])]});}
            var Q100;
            {var subQ0=sQuery(id+"F0.wireOp",EDGE,"E6.10.13.0");var subQ1=sQuery(id+"F0.wireOp",EDGE,"E6.3.13.0");var subQ2=makeQuery(id+"F0.imprint","INTERSECT",VERTEX,{"derivedFrom":[subQ1,subQ0]});Q100=makeQuery(id+"F0.imprint","IMPRINT",FACE,{"disambiguationData":[TD([[makeQuery(id+"F0.imprint","IMPRINT",EDGE,{"disambiguationData":[TD([[subQ2,1.0]])],"derivedFrom":subQ1}),-1.0]])]});}
            var Q101;
            {var subQ0=sQuery(id+"F0.wireOp",EDGE,"E6.6.13.0");var subQ1=sQuery(id+"F0.wireOp",EDGE,"E6.1.13.0");var subQ2=makeQuery(id+"F0.imprint","INTERSECT",VERTEX,{"derivedFrom":[subQ1,subQ0]});Q101=makeQuery(id+"F0.imprint","IMPRINT",FACE,{"disambiguationData":[TD([[makeQuery(id+"F0.imprint","IMPRINT",EDGE,{"disambiguationData":[TD([[subQ2,-1.0]])],"derivedFrom":subQ1}),1.0]])]});}
            var Q102;
            {var subQ0=sQuery(id+"F0.wireOp",EDGE,"E8");var subQ1=sQuery(id+"F0.wireOp",EDGE,"E6.1.16.0");var subQ2=makeQuery(id+"F0.imprint","INTERSECT",VERTEX,{"derivedFrom":[subQ1,subQ0]});Q102=makeQuery(id+"F0.imprint","IMPRINT",FACE,{"disambiguationData":[TD([[makeQuery(id+"F0.imprint","IMPRINT",EDGE,{"disambiguationData":[TD([[subQ2,-1.0]])],"derivedFrom":subQ1}),1.0]])]});}
            var Q103;
            {var subQ1=sQuery(id+"F0.wireOp",EDGE,"E6.1.10.0");var subQ3=sQuery(id+"F0.wireOp",EDGE,"E7");var subQ4=makeQuery(id+"F0.imprint","INTERSECT",VERTEX,{"derivedFrom":[subQ1,subQ3]});Q103=makeQuery(id+"F0.imprint","IMPRINT",FACE,{"disambiguationData":[TD([[makeQuery(id+"F0.imprint","IMPRINT",EDGE,{"disambiguationData":[TD([[subQ4,-1.0]])],"derivedFrom":subQ3}),1.0]])]});}
            var Q104;
            {var subQ1=sQuery(id+"F0.wireOp",EDGE,"E5.3.3.0");var subQ3=sQuery(id+"F0.wireOp",EDGE,"E8");var subQ4=makeQuery(id+"F0.imprint","INTERSECT",VERTEX,{"derivedFrom":[subQ1,subQ3]});Q104=makeQuery(id+"F0.imprint","IMPRINT",FACE,{"disambiguationData":[TD([[makeQuery(id+"F0.imprint","IMPRINT",EDGE,{"disambiguationData":[TD([[subQ4,-1.0]])],"derivedFrom":subQ3}),1.0]])]});}
            var Q105;
            {var subQ1=sQuery(id+"F0.wireOp",EDGE,"E6.3.17.0");var subQ3=sQuery(id+"F0.wireOp",EDGE,"E8");var subQ4=makeQuery(id+"F0.imprint","INTERSECT",VERTEX,{"derivedFrom":[subQ1,subQ3]});Q105=makeQuery(id+"F0.imprint","IMPRINT",FACE,{"disambiguationData":[TD([[makeQuery(id+"F0.imprint","IMPRINT",EDGE,{"disambiguationData":[TD([[subQ4,-1.0]])],"derivedFrom":subQ3}),1.0]])]});}
            var Q106;
            {var subQ1=sQuery(id+"F0.wireOp",EDGE,"E6.1.14.0");var subQ3=sQuery(id+"F0.wireOp",EDGE,"E7");var subQ4=makeQuery(id+"F0.imprint","INTERSECT",VERTEX,{"derivedFrom":[subQ1,subQ3]});Q106=makeQuery(id+"F0.imprint","IMPRINT",FACE,{"disambiguationData":[TD([[makeQuery(id+"F0.imprint","IMPRINT",EDGE,{"disambiguationData":[TD([[subQ4,-1.0]])],"derivedFrom":subQ3}),1.0]])]});}
            var Q107;
            {var subQ1=sQuery(id+"F0.wireOp",EDGE,"E6.3.10.0");var subQ3=sQuery(id+"F0.wireOp",EDGE,"E8");var subQ4=makeQuery(id+"F0.imprint","INTERSECT",VERTEX,{"derivedFrom":[subQ1,subQ3]});Q107=makeQuery(id+"F0.imprint","IMPRINT",FACE,{"disambiguationData":[TD([[makeQuery(id+"F0.imprint","IMPRINT",EDGE,{"disambiguationData":[TD([[subQ4,-1.0]])],"derivedFrom":subQ3}),1.0]])]});}
            var Q108;
            {var subQ1=sQuery(id+"F0.wireOp",EDGE,"E6.1.12.0");var subQ3=sQuery(id+"F0.wireOp",EDGE,"E7");var subQ4=makeQuery(id+"F0.imprint","INTERSECT",VERTEX,{"derivedFrom":[subQ1,subQ3]});Q108=makeQuery(id+"F0.imprint","IMPRINT",FACE,{"disambiguationData":[TD([[makeQuery(id+"F0.imprint","IMPRINT",EDGE,{"disambiguationData":[TD([[subQ4,-1.0]])],"derivedFrom":subQ3}),1.0]])]});}
            var Q109;
            {var subQ0=sQuery(id+"F0.wireOp",EDGE,"E5.10.7.0");var subQ3=sQuery(id+"F0.wireOp",EDGE,"E7");var subQ5=makeQuery(id+"F0.imprint","INTERSECT",VERTEX,{"derivedFrom":[subQ0,subQ3]});Q109=makeQuery(id+"F0.imprint","IMPRINT",FACE,{"disambiguationData":[TD([[makeQuery(id+"F0.imprint","IMPRINT",EDGE,{"disambiguationData":[TD([[subQ5,-1.0]])],"derivedFrom":subQ3}),1.0]])]});}
            var Q110;
            {var subQ0=sQuery(id+"F0.wireOp",EDGE,"E6.10.11.0");var subQ1=sQuery(id+"F0.wireOp",EDGE,"E6.3.11.0");var subQ2=makeQuery(id+"F0.imprint","INTERSECT",VERTEX,{"derivedFrom":[subQ1,subQ0]});Q110=makeQuery(id+"F0.imprint","IMPRINT",FACE,{"disambiguationData":[TD([[makeQuery(id+"F0.imprint","IMPRINT",EDGE,{"disambiguationData":[TD([[subQ2,1.0]])],"derivedFrom":subQ1}),-1.0]])]});}
            var Q111;
            {var subQ0=sQuery(id+"F0.wireOp",EDGE,"E8");var subQ1=sQuery(id+"F0.wireOp",EDGE,"E6.1.9.0");var subQ2=makeQuery(id+"F0.imprint","INTERSECT",VERTEX,{"derivedFrom":[subQ1,subQ0]});Q111=makeQuery(id+"F0.imprint","IMPRINT",FACE,{"disambiguationData":[TD([[makeQuery(id+"F0.imprint","IMPRINT",EDGE,{"disambiguationData":[TD([[subQ2,-1.0]])],"derivedFrom":subQ1}),-1.0]])]});}
            var Q112;
            {var subQ0=sQuery(id+"F0.wireOp",EDGE,"E8");var subQ1=sQuery(id+"F0.wireOp",EDGE,"E6.1.10.0");var subQ2=makeQuery(id+"F0.imprint","INTERSECT",VERTEX,{"derivedFrom":[subQ1,subQ0]});Q112=makeQuery(id+"F0.imprint","IMPRINT",FACE,{"disambiguationData":[TD([[makeQuery(id+"F0.imprint","IMPRINT",EDGE,{"disambiguationData":[TD([[subQ2,-1.0]])],"derivedFrom":subQ1}),-1.0]])]});}
            var Q113;
            {var subQ0=sQuery(id+"F0.wireOp",EDGE,"E5.10.5.0");var subQ3=sQuery(id+"F0.wireOp",EDGE,"E7");var subQ5=makeQuery(id+"F0.imprint","INTERSECT",VERTEX,{"derivedFrom":[subQ0,subQ3]});Q113=makeQuery(id+"F0.imprint","IMPRINT",FACE,{"disambiguationData":[TD([[makeQuery(id+"F0.imprint","IMPRINT",EDGE,{"disambiguationData":[TD([[subQ5,-1.0]])],"derivedFrom":subQ3}),1.0]])]});}
            var Q114;
            {var subQ0=sQuery(id+"F0.wireOp",EDGE,"E8");var subQ1=sQuery(id+"F0.wireOp",EDGE,"E6.1.13.0");var subQ2=makeQuery(id+"F0.imprint","INTERSECT",VERTEX,{"derivedFrom":[subQ1,subQ0]});Q114=makeQuery(id+"F0.imprint","IMPRINT",FACE,{"disambiguationData":[TD([[makeQuery(id+"F0.imprint","IMPRINT",EDGE,{"disambiguationData":[TD([[subQ2,-1.0]])],"derivedFrom":subQ1}),-1.0]])]});}
            var Q115;
            {var subQ0=sQuery(id+"F0.wireOp",EDGE,"E6.10.16.0");var subQ3=sQuery(id+"F0.wireOp",EDGE,"E7");var subQ5=makeQuery(id+"F0.imprint","INTERSECT",VERTEX,{"derivedFrom":[subQ0,subQ3]});Q115=makeQuery(id+"F0.imprint","IMPRINT",FACE,{"disambiguationData":[TD([[makeQuery(id+"F0.imprint","IMPRINT",EDGE,{"disambiguationData":[TD([[subQ5,-1.0]])],"derivedFrom":subQ3}),1.0]])]});}
            var Q116;
            {var subQ0=sQuery(id+"F0.wireOp",EDGE,"E8");var subQ1=sQuery(id+"F0.wireOp",EDGE,"E6.1.8.0");var subQ2=makeQuery(id+"F0.imprint","INTERSECT",VERTEX,{"derivedFrom":[subQ1,subQ0]});Q116=makeQuery(id+"F0.imprint","IMPRINT",FACE,{"disambiguationData":[TD([[makeQuery(id+"F0.imprint","IMPRINT",EDGE,{"disambiguationData":[TD([[subQ2,-1.0]])],"derivedFrom":subQ1}),1.0]])]});}
            var Q117;
            {var subQ3=sQuery(id+"F0.wireOp",EDGE,"E8");var subQ5=sQuery(id+"F0.wireOp",EDGE,"E6.10.16.0");var subQ6=makeQuery(id+"F0.imprint","INTERSECT",VERTEX,{"derivedFrom":[subQ5,subQ3]});Q117=makeQuery(id+"F0.imprint","IMPRINT",FACE,{"disambiguationData":[TD([[makeQuery(id+"F0.imprint","IMPRINT",EDGE,{"disambiguationData":[TD([[subQ6,1.0]])],"derivedFrom":subQ5}),1.0]])]});}
            var Q118;
            {var subQ3=sQuery(id+"F0.wireOp",EDGE,"E8");var subQ5=sQuery(id+"F0.wireOp",EDGE,"E5.10.6.0");var subQ6=makeQuery(id+"F0.imprint","INTERSECT",VERTEX,{"derivedFrom":[subQ5,subQ3]});Q118=makeQuery(id+"F0.imprint","IMPRINT",FACE,{"disambiguationData":[TD([[makeQuery(id+"F0.imprint","IMPRINT",EDGE,{"disambiguationData":[TD([[subQ6,1.0]])],"derivedFrom":subQ5}),1.0]])]});}
            var Q119;
            {var subQ0=sQuery(id+"F0.wireOp",EDGE,"E6.10.10.0");var subQ1=sQuery(id+"F0.wireOp",EDGE,"E6.3.10.0");var subQ2=makeQuery(id+"F0.imprint","INTERSECT",VERTEX,{"derivedFrom":[subQ1,subQ0]});Q119=makeQuery(id+"F0.imprint","IMPRINT",FACE,{"disambiguationData":[TD([[makeQuery(id+"F0.imprint","IMPRINT",EDGE,{"disambiguationData":[TD([[subQ2,1.0]])],"derivedFrom":subQ1}),-1.0]])]});}
            var Q120;
            {var subQ0=sQuery(id+"F0.wireOp",EDGE,"E6.6.11.0");var subQ1=sQuery(id+"F0.wireOp",EDGE,"E6.1.11.0");var subQ2=makeQuery(id+"F0.imprint","INTERSECT",VERTEX,{"derivedFrom":[subQ1,subQ0]});Q120=makeQuery(id+"F0.imprint","IMPRINT",FACE,{"disambiguationData":[TD([[makeQuery(id+"F0.imprint","IMPRINT",EDGE,{"disambiguationData":[TD([[subQ2,-1.0]])],"derivedFrom":subQ1}),1.0]])]});}
            var Q121;
            {var subQ0=sQuery(id+"F0.wireOp",EDGE,"E8");var subQ1=sQuery(id+"F0.wireOp",EDGE,"E4.2.0");var subQ2=makeQuery(id+"F0.imprint","INTERSECT",VERTEX,{"derivedFrom":[subQ1,subQ0]});Q121=makeQuery(id+"F0.imprint","IMPRINT",FACE,{"disambiguationData":[TD([[makeQuery(id+"F0.imprint","IMPRINT",EDGE,{"disambiguationData":[TD([[subQ2,-1.0]])],"derivedFrom":subQ1}),-1.0]])]});}
            var Q122;
            {var subQ0=sQuery(id+"F0.wireOp",EDGE,"E6.10.17.0");var subQ1=sQuery(id+"F0.wireOp",EDGE,"E6.3.17.0");var subQ2=makeQuery(id+"F0.imprint","INTERSECT",VERTEX,{"derivedFrom":[subQ1,subQ0]});Q122=makeQuery(id+"F0.imprint","IMPRINT",FACE,{"disambiguationData":[TD([[makeQuery(id+"F0.imprint","IMPRINT",EDGE,{"disambiguationData":[TD([[subQ2,1.0]])],"derivedFrom":subQ1}),-1.0]])]});}
            var Q123;
            {var subQ0=sQuery(id+"F0.wireOp",EDGE,"E8");var subQ1=sQuery(id+"F0.wireOp",EDGE,"E5.1.3.0");var subQ2=makeQuery(id+"F0.imprint","INTERSECT",VERTEX,{"derivedFrom":[subQ1,subQ0]});Q123=makeQuery(id+"F0.imprint","IMPRINT",FACE,{"disambiguationData":[TD([[makeQuery(id+"F0.imprint","IMPRINT",EDGE,{"disambiguationData":[TD([[subQ2,-1.0]])],"derivedFrom":subQ1}),1.0]])]});}
            var Q124;
            {var subQ3=sQuery(id+"F0.wireOp",EDGE,"E8");var subQ5=sQuery(id+"F0.wireOp",EDGE,"E5.10.7.0");var subQ6=makeQuery(id+"F0.imprint","INTERSECT",VERTEX,{"derivedFrom":[subQ5,subQ3]});Q124=makeQuery(id+"F0.imprint","IMPRINT",FACE,{"disambiguationData":[TD([[makeQuery(id+"F0.imprint","IMPRINT",EDGE,{"disambiguationData":[TD([[subQ6,1.0]])],"derivedFrom":subQ5}),1.0]])]});}
            var Q125;
            {var subQ0=sQuery(id+"F0.wireOp",EDGE,"E8");var subQ1=sQuery(id+"F0.wireOp",EDGE,"E1");var subQ2=makeQuery(id+"F0.imprint","INTERSECT",VERTEX,{"derivedFrom":[subQ1,subQ0]});Q125=makeQuery(id+"F0.imprint","IMPRINT",FACE,{"disambiguationData":[TD([[makeQuery(id+"F0.imprint","IMPRINT",EDGE,{"disambiguationData":[TD([[subQ2,-1.0]])],"derivedFrom":subQ1}),-1.0]])]});}
            var Q126;
            {var subQ0=sQuery(id+"F0.wireOp",EDGE,"E5.10.4.0");var subQ1=sQuery(id+"F0.wireOp",EDGE,"E5.3.4.0");var subQ2=makeQuery(id+"F0.imprint","INTERSECT",VERTEX,{"derivedFrom":[subQ1,subQ0]});Q126=makeQuery(id+"F0.imprint","IMPRINT",FACE,{"disambiguationData":[TD([[makeQuery(id+"F0.imprint","IMPRINT",EDGE,{"disambiguationData":[TD([[subQ2,1.0]])],"derivedFrom":subQ1}),-1.0]])]});}
            var Q127;
            {var subQ3=sQuery(id+"F0.wireOp",EDGE,"E8");var subQ5=sQuery(id+"F0.wireOp",EDGE,"E6.10.9.0");var subQ6=makeQuery(id+"F0.imprint","INTERSECT",VERTEX,{"derivedFrom":[subQ5,subQ3]});Q127=makeQuery(id+"F0.imprint","IMPRINT",FACE,{"disambiguationData":[TD([[makeQuery(id+"F0.imprint","IMPRINT",EDGE,{"disambiguationData":[TD([[subQ6,1.0]])],"derivedFrom":subQ5}),1.0]])]});}
            var Q128;
            {var subQ0=sQuery(id+"F0.wireOp",EDGE,"E8");var subQ1=sQuery(id+"F0.wireOp",EDGE,"E6.1.11.0");var subQ2=makeQuery(id+"F0.imprint","INTERSECT",VERTEX,{"derivedFrom":[subQ1,subQ0]});Q128=makeQuery(id+"F0.imprint","IMPRINT",FACE,{"disambiguationData":[TD([[makeQuery(id+"F0.imprint","IMPRINT",EDGE,{"disambiguationData":[TD([[subQ2,-1.0]])],"derivedFrom":subQ1}),-1.0]])]});}
            var Q129;
            {var subQ0=sQuery(id+"F0.wireOp",EDGE,"E8");var subQ1=sQuery(id+"F0.wireOp",EDGE,"E5.1.7.0");var subQ2=makeQuery(id+"F0.imprint","INTERSECT",VERTEX,{"derivedFrom":[subQ1,subQ0]});Q129=makeQuery(id+"F0.imprint","IMPRINT",FACE,{"disambiguationData":[TD([[makeQuery(id+"F0.imprint","IMPRINT",EDGE,{"disambiguationData":[TD([[subQ2,-1.0]])],"derivedFrom":subQ1}),-1.0]])]});}
            var Q130;
            {var subQ0=sQuery(id+"F0.wireOp",EDGE,"E6.10.15.0");var subQ3=sQuery(id+"F0.wireOp",EDGE,"E7");var subQ5=makeQuery(id+"F0.imprint","INTERSECT",VERTEX,{"derivedFrom":[subQ0,subQ3]});Q130=makeQuery(id+"F0.imprint","IMPRINT",FACE,{"disambiguationData":[TD([[makeQuery(id+"F0.imprint","IMPRINT",EDGE,{"disambiguationData":[TD([[subQ5,-1.0]])],"derivedFrom":subQ3}),1.0]])]});}
            var Q131;
            {var subQ1=sQuery(id+"F0.wireOp",EDGE,"E0");var subQ3=sQuery(id+"F0.wireOp",EDGE,"E7");var subQ4=makeQuery(id+"F0.imprint","INTERSECT",VERTEX,{"derivedFrom":[subQ1,subQ3]});Q131=makeQuery(id+"F0.imprint","IMPRINT",FACE,{"disambiguationData":[TD([[makeQuery(id+"F0.imprint","IMPRINT",EDGE,{"disambiguationData":[TD([[subQ4,-1.0]])],"derivedFrom":subQ3}),1.0]])]});}
            var Q132;
            {var subQ1=sQuery(id+"F0.wireOp",EDGE,"E5.1.4.0");var subQ3=sQuery(id+"F0.wireOp",EDGE,"E7");var subQ4=makeQuery(id+"F0.imprint","INTERSECT",VERTEX,{"derivedFrom":[subQ1,subQ3]});Q132=makeQuery(id+"F0.imprint","IMPRINT",FACE,{"disambiguationData":[TD([[makeQuery(id+"F0.imprint","IMPRINT",EDGE,{"disambiguationData":[TD([[subQ4,-1.0]])],"derivedFrom":subQ3}),1.0]])]});}
            var Q133;
            {var subQ0=sQuery(id+"F0.wireOp",EDGE,"E4.1.4");var subQ1=sQuery(id+"F0.wireOp",EDGE,"E4.1.1");var subQ2=makeQuery(id+"F0.imprint","INTERSECT",VERTEX,{"derivedFrom":[subQ1,subQ0]});Q133=makeQuery(id+"F0.imprint","IMPRINT",FACE,{"disambiguationData":[TD([[makeQuery(id+"F0.imprint","IMPRINT",EDGE,{"disambiguationData":[TD([[subQ2,1.0]])],"derivedFrom":subQ1}),-1.0]])]});}
            var Q134;
            {var subQ0=sQuery(id+"F0.wireOp",EDGE,"E6.10.14.0");var subQ1=sQuery(id+"F0.wireOp",EDGE,"E6.3.14.0");var subQ2=makeQuery(id+"F0.imprint","INTERSECT",VERTEX,{"derivedFrom":[subQ1,subQ0]});Q134=makeQuery(id+"F0.imprint","IMPRINT",FACE,{"disambiguationData":[TD([[makeQuery(id+"F0.imprint","IMPRINT",EDGE,{"disambiguationData":[TD([[subQ2,1.0]])],"derivedFrom":subQ1}),-1.0]])]});}
            var Q135;
            {var subQ1=sQuery(id+"F0.wireOp",EDGE,"E5.3.5.0");var subQ3=sQuery(id+"F0.wireOp",EDGE,"E8");var subQ4=makeQuery(id+"F0.imprint","INTERSECT",VERTEX,{"derivedFrom":[subQ1,subQ3]});Q135=makeQuery(id+"F0.imprint","IMPRINT",FACE,{"disambiguationData":[TD([[makeQuery(id+"F0.imprint","IMPRINT",EDGE,{"disambiguationData":[TD([[subQ4,-1.0]])],"derivedFrom":subQ3}),1.0]])]});}
            var Q136;
            {var subQ0=sQuery(id+"F0.wireOp",EDGE,"E6.6.10.0");var subQ1=sQuery(id+"F0.wireOp",EDGE,"E6.1.10.0");var subQ2=makeQuery(id+"F0.imprint","INTERSECT",VERTEX,{"derivedFrom":[subQ1,subQ0]});Q136=makeQuery(id+"F0.imprint","IMPRINT",FACE,{"disambiguationData":[TD([[makeQuery(id+"F0.imprint","IMPRINT",EDGE,{"disambiguationData":[TD([[subQ2,-1.0]])],"derivedFrom":subQ1}),1.0]])]});}
            var Q137;
            {var subQ0=sQuery(id+"F0.wireOp",EDGE,"E6.10.15.0");var subQ1=sQuery(id+"F0.wireOp",EDGE,"E6.3.15.0");var subQ2=makeQuery(id+"F0.imprint","INTERSECT",VERTEX,{"derivedFrom":[subQ1,subQ0]});Q137=makeQuery(id+"F0.imprint","IMPRINT",FACE,{"disambiguationData":[TD([[makeQuery(id+"F0.imprint","IMPRINT",EDGE,{"disambiguationData":[TD([[subQ2,1.0]])],"derivedFrom":subQ1}),-1.0]])]});}
            var Q138;
            {var subQ0=sQuery(id+"F0.wireOp",EDGE,"E6.10.10.0");var subQ3=sQuery(id+"F0.wireOp",EDGE,"E7");var subQ5=makeQuery(id+"F0.imprint","INTERSECT",VERTEX,{"derivedFrom":[subQ0,subQ3]});Q138=makeQuery(id+"F0.imprint","IMPRINT",FACE,{"disambiguationData":[TD([[makeQuery(id+"F0.imprint","IMPRINT",EDGE,{"disambiguationData":[TD([[subQ5,-1.0]])],"derivedFrom":subQ3}),1.0]])]});}
            var Q139;
            {var subQ0=sQuery(id+"F0.wireOp",EDGE,"E8");var subQ1=sQuery(id+"F0.wireOp",EDGE,"E6.1.11.0");var subQ2=makeQuery(id+"F0.imprint","INTERSECT",VERTEX,{"derivedFrom":[subQ1,subQ0]});Q139=makeQuery(id+"F0.imprint","IMPRINT",FACE,{"disambiguationData":[TD([[makeQuery(id+"F0.imprint","IMPRINT",EDGE,{"disambiguationData":[TD([[subQ2,-1.0]])],"derivedFrom":subQ1}),1.0]])]});}
            var Q140;
            {var subQ1=sQuery(id+"F0.wireOp",EDGE,"E6.3.15.0");var subQ3=sQuery(id+"F0.wireOp",EDGE,"E8");var subQ4=makeQuery(id+"F0.imprint","INTERSECT",VERTEX,{"derivedFrom":[subQ1,subQ3]});Q140=makeQuery(id+"F0.imprint","IMPRINT",FACE,{"disambiguationData":[TD([[makeQuery(id+"F0.imprint","IMPRINT",EDGE,{"disambiguationData":[TD([[subQ4,-1.0]])],"derivedFrom":subQ3}),1.0]])]});}
            var Q141;
            {var subQ1=sQuery(id+"F0.wireOp",EDGE,"E5.3.4.0");var subQ3=sQuery(id+"F0.wireOp",EDGE,"E8");var subQ4=makeQuery(id+"F0.imprint","INTERSECT",VERTEX,{"derivedFrom":[subQ1,subQ3]});Q141=makeQuery(id+"F0.imprint","IMPRINT",FACE,{"disambiguationData":[TD([[makeQuery(id+"F0.imprint","IMPRINT",EDGE,{"disambiguationData":[TD([[subQ4,-1.0]])],"derivedFrom":subQ3}),1.0]])]});}
            extrude(context, id + "F1", {"entities" : qUnion([Q0, Q1, Q2, Q3, Q4, Q5, Q6, Q7, Q8, Q9, Q10, Q11, Q12, Q13, Q14, Q15, Q16, Q17, Q18, Q19, Q20, Q21, Q22, Q23, Q24, Q25, Q26, Q27, Q28, Q29, Q30, Q31, Q32, Q33, Q34, Q35, Q36, Q37, Q38, Q39, Q40, Q41, Q42, Q43, Q44, Q45, Q46, Q47, Q48, Q49, Q50, Q51, Q52, Q53, Q54, Q55, Q56, Q57, Q58, Q59, Q60, Q61, Q62, Q63, Q64, Q65, Q66, Q67, Q68, Q69, Q70, Q71, Q72, Q73, Q74, Q75, Q76, Q77, Q78, Q79, Q80, Q81, Q82, Q83, Q84, Q85, Q86, Q87, Q88, Q89, Q90, Q91, Q92, Q93, Q94, Q95, Q96, Q97, Q98, Q99, Q100, Q101, Q102, Q103, Q104, Q105, Q106, Q107, Q108, Q109, Q110, Q111, Q112, Q113, Q114, Q115, Q116, Q117, Q118, Q119, Q120, Q121, Q122, Q123, Q124, Q125, Q126, Q127, Q128, Q129, Q130, Q131, Q132, Q133, Q134, Q135, Q136, Q137, Q138, Q139, Q140, Q141]), "depth" : 12 * mm, "offsetDistance" : 25 * mm, "hasDraft" : true, "draftAngle" : 5 * degree, "draftPullDirection" : true});
        }
        {
            var Q0;
            {var subQ0=sQuery(id+"F0.wireOp",EDGE,"E8");Q0=makeQuery(id+"F1.*.draft.opDraft","MERGE",EDGE,{"derivedFrom":[makeQuery(id+"F1.opExtrude","CAP_EDGE",EDGE,{"disambiguationData":[OSD([subQ0]),TDD([makeQuery(id+"F0.imprint","IMPRINT",EDGE,{"disambiguationData":[TD([[makeQuery(id+"F0.imprint","INTERSECT",VERTEX,{"derivedFrom":[sQuery(id+"F0.wireOp",EDGE,"E6.3.14.0"),subQ0]}),-1.0]])],"derivedFrom":subQ0})])],"isStart":false}),makeQuery(id+"F1.opExtrude","CAP_EDGE",EDGE,{"disambiguationData":[OSD([subQ0]),TDD([makeQuery(id+"F0.imprint","IMPRINT",EDGE,{"disambiguationData":[TD([[makeQuery(id+"F0.imprint","INTERSECT",VERTEX,{"derivedFrom":[sQuery(id+"F0.wireOp",EDGE,"E6.1.14.0"),subQ0]}),-1.0]])],"derivedFrom":subQ0})])],"isStart":false}),makeQuery(id+"F1.opExtrude","CAP_EDGE",EDGE,{"disambiguationData":[OSD([subQ0]),TDD([makeQuery(id+"F0.imprint","IMPRINT",EDGE,{"disambiguationData":[TD([[makeQuery(id+"F0.imprint","INTERSECT",VERTEX,{"derivedFrom":[sQuery(id+"F0.wireOp",EDGE,"E6.3.15.0"),subQ0]}),-1.0]])],"derivedFrom":subQ0})])],"isStart":false}),makeQuery(id+"F1.opExtrude","CAP_EDGE",EDGE,{"disambiguationData":[OSD([subQ0]),TDD([makeQuery(id+"F0.imprint","IMPRINT",EDGE,{"disambiguationData":[TD([[makeQuery(id+"F0.imprint","INTERSECT",VERTEX,{"derivedFrom":[sQuery(id+"F0.wireOp",EDGE,"E6.1.15.0"),subQ0]}),-1.0]])],"derivedFrom":subQ0})])],"isStart":false}),makeQuery(id+"F1.opExtrude","CAP_EDGE",EDGE,{"disambiguationData":[OSD([subQ0]),TDD([makeQuery(id+"F0.imprint","IMPRINT",EDGE,{"disambiguationData":[TD([[makeQuery(id+"F0.imprint","INTERSECT",VERTEX,{"derivedFrom":[sQuery(id+"F0.wireOp",EDGE,"E6.3.16.0"),subQ0]}),-1.0]])],"derivedFrom":subQ0})])],"isStart":false}),makeQuery(id+"F1.opExtrude","CAP_EDGE",EDGE,{"disambiguationData":[OSD([subQ0]),TDD([makeQuery(id+"F0.imprint","IMPRINT",EDGE,{"disambiguationData":[TD([[makeQuery(id+"F0.imprint","INTERSECT",VERTEX,{"derivedFrom":[sQuery(id+"F0.wireOp",EDGE,"E6.1.16.0"),subQ0]}),-1.0]])],"derivedFrom":subQ0})])],"isStart":false}),makeQuery(id+"F1.opExtrude","CAP_EDGE",EDGE,{"disambiguationData":[OSD([subQ0]),TDD([makeQuery(id+"F0.imprint","IMPRINT",EDGE,{"disambiguationData":[TD([[makeQuery(id+"F0.imprint","INTERSECT",VERTEX,{"derivedFrom":[sQuery(id+"F0.wireOp",EDGE,"E6.3.17.0"),subQ0]}),-1.0]])],"derivedFrom":subQ0})])],"isStart":false}),makeQuery(id+"F1.opExtrude","CAP_EDGE",EDGE,{"disambiguationData":[OSD([subQ0]),TDD([makeQuery(id+"F0.imprint","IMPRINT",EDGE,{"disambiguationData":[TD([[makeQuery(id+"F0.imprint","INTERSECT",VERTEX,{"derivedFrom":[sQuery(id+"F0.wireOp",EDGE,"E0"),subQ0]}),1.0]])],"derivedFrom":subQ0})])],"isStart":false}),makeQuery(id+"F1.opExtrude","CAP_EDGE",EDGE,{"disambiguationData":[OSD([subQ0]),TDD([makeQuery(id+"F0.imprint","IMPRINT",EDGE,{"disambiguationData":[TD([[makeQuery(id+"F0.imprint","INTERSECT",VERTEX,{"derivedFrom":[sQuery(id+"F0.wireOp",EDGE,"E2"),subQ0]}),1.0]])],"derivedFrom":subQ0})])],"isStart":false}),makeQuery(id+"F1.opExtrude","CAP_EDGE",EDGE,{"disambiguationData":[OSD([subQ0]),TDD([makeQuery(id+"F0.imprint","IMPRINT",EDGE,{"disambiguationData":[TD([[makeQuery(id+"F0.imprint","INTERSECT",VERTEX,{"derivedFrom":[sQuery(id+"F0.wireOp",EDGE,"E1"),subQ0]}),-1.0]])],"derivedFrom":subQ0})])],"isStart":false}),makeQuery(id+"F1.opExtrude","CAP_EDGE",EDGE,{"disambiguationData":[OSD([subQ0]),TDD([makeQuery(id+"F0.imprint","IMPRINT",EDGE,{"disambiguationData":[TD([[makeQuery(id+"F0.imprint","INTERSECT",VERTEX,{"derivedFrom":[sQuery(id+"F0.wireOp",EDGE,"E4.1.1"),subQ0]}),-1.0]])],"derivedFrom":subQ0})])],"isStart":false}),makeQuery(id+"F1.opExtrude","CAP_EDGE",EDGE,{"disambiguationData":[OSD([subQ0]),TDD([makeQuery(id+"F0.imprint","IMPRINT",EDGE,{"disambiguationData":[TD([[makeQuery(id+"F0.imprint","INTERSECT",VERTEX,{"derivedFrom":[sQuery(id+"F0.wireOp",EDGE,"E4.1.0"),subQ0]}),-1.0]])],"derivedFrom":subQ0})])],"isStart":false}),makeQuery(id+"F1.opExtrude","CAP_EDGE",EDGE,{"disambiguationData":[OSD([subQ0]),TDD([makeQuery(id+"F0.imprint","IMPRINT",EDGE,{"disambiguationData":[TD([[makeQuery(id+"F0.imprint","INTERSECT",VERTEX,{"derivedFrom":[sQuery(id+"F0.wireOp",EDGE,"E4.2.1"),subQ0]}),-1.0]])],"derivedFrom":subQ0})])],"isStart":false}),makeQuery(id+"F1.opExtrude","CAP_EDGE",EDGE,{"disambiguationData":[OSD([subQ0]),TDD([makeQuery(id+"F0.imprint","IMPRINT",EDGE,{"disambiguationData":[TD([[makeQuery(id+"F0.imprint","INTERSECT",VERTEX,{"derivedFrom":[sQuery(id+"F0.wireOp",EDGE,"E4.2.0"),subQ0]}),-1.0]])],"derivedFrom":subQ0})])],"isStart":false}),makeQuery(id+"F1.opExtrude","CAP_EDGE",EDGE,{"disambiguationData":[OSD([subQ0]),TDD([makeQuery(id+"F0.imprint","IMPRINT",EDGE,{"disambiguationData":[TD([[makeQuery(id+"F0.imprint","INTERSECT",VERTEX,{"derivedFrom":[sQuery(id+"F0.wireOp",EDGE,"E5.3.3.0"),subQ0]}),-1.0]])],"derivedFrom":subQ0})])],"isStart":false}),makeQuery(id+"F1.opExtrude","CAP_EDGE",EDGE,{"disambiguationData":[OSD([subQ0]),TDD([makeQuery(id+"F0.imprint","IMPRINT",EDGE,{"disambiguationData":[TD([[makeQuery(id+"F0.imprint","INTERSECT",VERTEX,{"derivedFrom":[sQuery(id+"F0.wireOp",EDGE,"E5.1.3.0"),subQ0]}),-1.0]])],"derivedFrom":subQ0})])],"isStart":false}),makeQuery(id+"F1.opExtrude","CAP_EDGE",EDGE,{"disambiguationData":[OSD([subQ0]),TDD([makeQuery(id+"F0.imprint","IMPRINT",EDGE,{"disambiguationData":[TD([[makeQuery(id+"F0.imprint","INTERSECT",VERTEX,{"derivedFrom":[sQuery(id+"F0.wireOp",EDGE,"E5.3.4.0"),subQ0]}),-1.0]])],"derivedFrom":subQ0})])],"isStart":false}),makeQuery(id+"F1.opExtrude","CAP_EDGE",EDGE,{"disambiguationData":[OSD([subQ0]),TDD([makeQuery(id+"F0.imprint","IMPRINT",EDGE,{"disambiguationData":[TD([[makeQuery(id+"F0.imprint","INTERSECT",VERTEX,{"derivedFrom":[sQuery(id+"F0.wireOp",EDGE,"E5.1.4.0"),subQ0]}),-1.0]])],"derivedFrom":subQ0})])],"isStart":false}),makeQuery(id+"F1.opExtrude","CAP_EDGE",EDGE,{"disambiguationData":[OSD([subQ0]),TDD([makeQuery(id+"F0.imprint","IMPRINT",EDGE,{"disambiguationData":[TD([[makeQuery(id+"F0.imprint","INTERSECT",VERTEX,{"derivedFrom":[sQuery(id+"F0.wireOp",EDGE,"E5.3.5.0"),subQ0]}),-1.0]])],"derivedFrom":subQ0})])],"isStart":false}),makeQuery(id+"F1.opExtrude","CAP_EDGE",EDGE,{"disambiguationData":[OSD([subQ0]),TDD([makeQuery(id+"F0.imprint","IMPRINT",EDGE,{"disambiguationData":[TD([[makeQuery(id+"F0.imprint","INTERSECT",VERTEX,{"derivedFrom":[sQuery(id+"F0.wireOp",EDGE,"E5.1.5.0"),subQ0]}),-1.0]])],"derivedFrom":subQ0})])],"isStart":false}),makeQuery(id+"F1.opExtrude","CAP_EDGE",EDGE,{"disambiguationData":[OSD([subQ0]),TDD([makeQuery(id+"F0.imprint","IMPRINT",EDGE,{"disambiguationData":[TD([[makeQuery(id+"F0.imprint","INTERSECT",VERTEX,{"derivedFrom":[sQuery(id+"F0.wireOp",EDGE,"E5.3.6.0"),subQ0]}),-1.0]])],"derivedFrom":subQ0})])],"isStart":false}),makeQuery(id+"F1.opExtrude","CAP_EDGE",EDGE,{"disambiguationData":[OSD([subQ0]),TDD([makeQuery(id+"F0.imprint","IMPRINT",EDGE,{"disambiguationData":[TD([[makeQuery(id+"F0.imprint","INTERSECT",VERTEX,{"derivedFrom":[sQuery(id+"F0.wireOp",EDGE,"E5.1.6.0"),subQ0]}),-1.0]])],"derivedFrom":subQ0})])],"isStart":false}),makeQuery(id+"F1.opExtrude","CAP_EDGE",EDGE,{"disambiguationData":[OSD([subQ0]),TDD([makeQuery(id+"F0.imprint","IMPRINT",EDGE,{"disambiguationData":[TD([[makeQuery(id+"F0.imprint","INTERSECT",VERTEX,{"derivedFrom":[sQuery(id+"F0.wireOp",EDGE,"E5.3.7.0"),subQ0]}),-1.0]])],"derivedFrom":subQ0})])],"isStart":false}),makeQuery(id+"F1.opExtrude","CAP_EDGE",EDGE,{"disambiguationData":[OSD([subQ0]),TDD([makeQuery(id+"F0.imprint","IMPRINT",EDGE,{"disambiguationData":[TD([[makeQuery(id+"F0.imprint","INTERSECT",VERTEX,{"derivedFrom":[sQuery(id+"F0.wireOp",EDGE,"E5.1.7.0"),subQ0]}),-1.0]])],"derivedFrom":subQ0})])],"isStart":false}),makeQuery(id+"F1.opExtrude","CAP_EDGE",EDGE,{"disambiguationData":[OSD([subQ0]),TDD([makeQuery(id+"F0.imprint","IMPRINT",EDGE,{"disambiguationData":[TD([[makeQuery(id+"F0.imprint","INTERSECT",VERTEX,{"derivedFrom":[sQuery(id+"F0.wireOp",EDGE,"E6.3.8.0"),subQ0]}),-1.0]])],"derivedFrom":subQ0})])],"isStart":false}),makeQuery(id+"F1.opExtrude","CAP_EDGE",EDGE,{"disambiguationData":[OSD([subQ0]),TDD([makeQuery(id+"F0.imprint","IMPRINT",EDGE,{"disambiguationData":[TD([[makeQuery(id+"F0.imprint","INTERSECT",VERTEX,{"derivedFrom":[sQuery(id+"F0.wireOp",EDGE,"E6.1.8.0"),subQ0]}),-1.0]])],"derivedFrom":subQ0})])],"isStart":false}),makeQuery(id+"F1.opExtrude","CAP_EDGE",EDGE,{"disambiguationData":[OSD([subQ0]),TDD([makeQuery(id+"F0.imprint","IMPRINT",EDGE,{"disambiguationData":[TD([[makeQuery(id+"F0.imprint","INTERSECT",VERTEX,{"derivedFrom":[sQuery(id+"F0.wireOp",EDGE,"E6.3.9.0"),subQ0]}),-1.0]])],"derivedFrom":subQ0})])],"isStart":false}),makeQuery(id+"F1.opExtrude","CAP_EDGE",EDGE,{"disambiguationData":[OSD([subQ0]),TDD([makeQuery(id+"F0.imprint","IMPRINT",EDGE,{"disambiguationData":[TD([[makeQuery(id+"F0.imprint","INTERSECT",VERTEX,{"derivedFrom":[sQuery(id+"F0.wireOp",EDGE,"E6.1.9.0"),subQ0]}),-1.0]])],"derivedFrom":subQ0})])],"isStart":false}),makeQuery(id+"F1.opExtrude","CAP_EDGE",EDGE,{"disambiguationData":[OSD([subQ0]),TDD([makeQuery(id+"F0.imprint","IMPRINT",EDGE,{"disambiguationData":[TD([[makeQuery(id+"F0.imprint","INTERSECT",VERTEX,{"derivedFrom":[sQuery(id+"F0.wireOp",EDGE,"E6.3.10.0"),subQ0]}),-1.0]])],"derivedFrom":subQ0})])],"isStart":false}),makeQuery(id+"F1.opExtrude","CAP_EDGE",EDGE,{"disambiguationData":[OSD([subQ0]),TDD([makeQuery(id+"F0.imprint","IMPRINT",EDGE,{"disambiguationData":[TD([[makeQuery(id+"F0.imprint","INTERSECT",VERTEX,{"derivedFrom":[sQuery(id+"F0.wireOp",EDGE,"E6.1.10.0"),subQ0]}),-1.0]])],"derivedFrom":subQ0})])],"isStart":false}),makeQuery(id+"F1.opExtrude","CAP_EDGE",EDGE,{"disambiguationData":[OSD([subQ0]),TDD([makeQuery(id+"F0.imprint","IMPRINT",EDGE,{"disambiguationData":[TD([[makeQuery(id+"F0.imprint","INTERSECT",VERTEX,{"derivedFrom":[sQuery(id+"F0.wireOp",EDGE,"E6.3.11.0"),subQ0]}),-1.0]])],"derivedFrom":subQ0})])],"isStart":false}),makeQuery(id+"F1.opExtrude","CAP_EDGE",EDGE,{"disambiguationData":[OSD([subQ0]),TDD([makeQuery(id+"F0.imprint","IMPRINT",EDGE,{"disambiguationData":[TD([[makeQuery(id+"F0.imprint","INTERSECT",VERTEX,{"derivedFrom":[sQuery(id+"F0.wireOp",EDGE,"E6.1.11.0"),subQ0]}),-1.0]])],"derivedFrom":subQ0})])],"isStart":false}),makeQuery(id+"F1.opExtrude","CAP_EDGE",EDGE,{"disambiguationData":[OSD([subQ0]),TDD([makeQuery(id+"F0.imprint","IMPRINT",EDGE,{"disambiguationData":[TD([[makeQuery(id+"F0.imprint","INTERSECT",VERTEX,{"derivedFrom":[sQuery(id+"F0.wireOp",EDGE,"E6.3.12.0"),subQ0]}),-1.0]])],"derivedFrom":subQ0})])],"isStart":false}),makeQuery(id+"F1.opExtrude","CAP_EDGE",EDGE,{"disambiguationData":[OSD([subQ0]),TDD([makeQuery(id+"F0.imprint","IMPRINT",EDGE,{"disambiguationData":[TD([[makeQuery(id+"F0.imprint","INTERSECT",VERTEX,{"derivedFrom":[sQuery(id+"F0.wireOp",EDGE,"E6.1.12.0"),subQ0]}),-1.0]])],"derivedFrom":subQ0})])],"isStart":false}),makeQuery(id+"F1.opExtrude","CAP_EDGE",EDGE,{"disambiguationData":[OSD([subQ0]),TDD([makeQuery(id+"F0.imprint","IMPRINT",EDGE,{"disambiguationData":[TD([[makeQuery(id+"F0.imprint","INTERSECT",VERTEX,{"derivedFrom":[sQuery(id+"F0.wireOp",EDGE,"E6.3.13.0"),subQ0]}),-1.0]])],"derivedFrom":subQ0})])],"isStart":false}),makeQuery(id+"F1.opExtrude","CAP_EDGE",EDGE,{"disambiguationData":[OSD([subQ0]),TDD([makeQuery(id+"F0.imprint","IMPRINT",EDGE,{"disambiguationData":[TD([[makeQuery(id+"F0.imprint","INTERSECT",VERTEX,{"derivedFrom":[sQuery(id+"F0.wireOp",EDGE,"E6.1.13.0"),subQ0]}),-1.0]])],"derivedFrom":subQ0})])],"isStart":false})]});}
            fillet(context, id + "F2", {"entities" : qUnion([Q0]), "radius" : 3 * mm, "tangentPropagation" : true, "allowEdgeOverflow" : false});
        }
        {
            var Q0;
            Q0=makeQuery(id+"F1.opExtrude","CAP_FACE",FACE,{"disambiguationData":[OSD([sQuery(id+"F0.wireOp",EDGE,"E0"),sQuery(id+"F0.wireOp",EDGE,"E1"),sQuery(id+"F0.wireOp",EDGE,"E2"),sQuery(id+"F0.wireOp",EDGE,"E3"),sQuery(id+"F0.wireOp",EDGE,"E4.1.0"),sQuery(id+"F0.wireOp",EDGE,"E4.1.1"),sQuery(id+"F0.wireOp",EDGE,"E4.1.2"),sQuery(id+"F0.wireOp",EDGE,"E4.1.4"),sQuery(id+"F0.wireOp",EDGE,"E4.2.0"),sQuery(id+"F0.wireOp",EDGE,"E4.2.1"),sQuery(id+"F0.wireOp",EDGE,"E4.2.2"),sQuery(id+"F0.wireOp",EDGE,"E4.2.4"),sQuery(id+"F0.wireOp",EDGE,"E5.1.3.0"),sQuery(id+"F0.wireOp",EDGE,"E5.3.3.0"),sQuery(id+"F0.wireOp",EDGE,"E5.6.3.0"),sQuery(id+"F0.wireOp",EDGE,"E5.10.3.0"),sQuery(id+"F0.wireOp",EDGE,"E5.1.4.0"),sQuery(id+"F0.wireOp",EDGE,"E5.3.4.0"),sQuery(id+"F0.wireOp",EDGE,"E5.6.4.0"),sQuery(id+"F0.wireOp",EDGE,"E5.10.4.0"),sQuery(id+"F0.wireOp",EDGE,"E5.1.5.0"),sQuery(id+"F0.wireOp",EDGE,"E5.3.5.0"),sQuery(id+"F0.wireOp",EDGE,"E5.6.5.0"),sQuery(id+"F0.wireOp",EDGE,"E5.10.5.0"),sQuery(id+"F0.wireOp",EDGE,"E5.1.6.0"),sQuery(id+"F0.wireOp",EDGE,"E5.3.6.0"),sQuery(id+"F0.wireOp",EDGE,"E5.6.6.0"),sQuery(id+"F0.wireOp",EDGE,"E5.10.6.0"),sQuery(id+"F0.wireOp",EDGE,"E5.1.7.0"),sQuery(id+"F0.wireOp",EDGE,"E5.3.7.0"),sQuery(id+"F0.wireOp",EDGE,"E5.6.7.0"),sQuery(id+"F0.wireOp",EDGE,"E5.10.7.0"),sQuery(id+"F0.wireOp",EDGE,"E6.1.8.0"),sQuery(id+"F0.wireOp",EDGE,"E6.3.8.0"),sQuery(id+"F0.wireOp",EDGE,"E6.6.8.0"),sQuery(id+"F0.wireOp",EDGE,"E6.10.8.0"),sQuery(id+"F0.wireOp",EDGE,"E6.1.9.0"),sQuery(id+"F0.wireOp",EDGE,"E6.3.9.0"),sQuery(id+"F0.wireOp",EDGE,"E6.6.9.0"),sQuery(id+"F0.wireOp",EDGE,"E6.10.9.0"),sQuery(id+"F0.wireOp",EDGE,"E6.1.10.0"),sQuery(id+"F0.wireOp",EDGE,"E6.3.10.0"),sQuery(id+"F0.wireOp",EDGE,"E6.6.10.0"),sQuery(id+"F0.wireOp",EDGE,"E6.10.10.0"),sQuery(id+"F0.wireOp",EDGE,"E6.1.11.0"),sQuery(id+"F0.wireOp",EDGE,"E6.3.11.0"),sQuery(id+"F0.wireOp",EDGE,"E6.6.11.0"),sQuery(id+"F0.wireOp",EDGE,"E6.10.11.0"),sQuery(id+"F0.wireOp",EDGE,"E6.1.12.0"),sQuery(id+"F0.wireOp",EDGE,"E6.3.12.0"),sQuery(id+"F0.wireOp",EDGE,"E6.6.12.0"),sQuery(id+"F0.wireOp",EDGE,"E6.10.12.0"),sQuery(id+"F0.wireOp",EDGE,"E6.1.13.0"),sQuery(id+"F0.wireOp",EDGE,"E6.3.13.0"),sQuery(id+"F0.wireOp",EDGE,"E6.6.13.0"),sQuery(id+"F0.wireOp",EDGE,"E6.10.13.0"),sQuery(id+"F0.wireOp",EDGE,"E6.1.14.0"),sQuery(id+"F0.wireOp",EDGE,"E6.3.14.0"),sQuery(id+"F0.wireOp",EDGE,"E6.6.14.0"),sQuery(id+"F0.wireOp",EDGE,"E6.10.14.0"),sQuery(id+"F0.wireOp",EDGE,"E6.1.15.0"),sQuery(id+"F0.wireOp",EDGE,"E6.3.15.0"),sQuery(id+"F0.wireOp",EDGE,"E6.6.15.0"),sQuery(id+"F0.wireOp",EDGE,"E6.10.15.0"),sQuery(id+"F0.wireOp",EDGE,"E6.1.16.0"),sQuery(id+"F0.wireOp",EDGE,"E6.3.16.0"),sQuery(id+"F0.wireOp",EDGE,"E6.6.16.0"),sQuery(id+"F0.wireOp",EDGE,"E6.10.16.0"),sQuery(id+"F0.wireOp",EDGE,"E6.1.17.0"),sQuery(id+"F0.wireOp",EDGE,"E6.3.17.0"),sQuery(id+"F0.wireOp",EDGE,"E6.6.17.0"),sQuery(id+"F0.wireOp",EDGE,"E6.10.17.0"),sQuery(id+"F0.wireOp",EDGE,"E8")])],"isStart":true});
            var sketch = newSketch(context, id + "F3", { "sketchPlane" : qUnion([Q0])});
            skCircle(sketch, "E9", {"center": v(0, 0) * mm, "radius": 5 * mm});
            skCircle(sketch, "E10", {"center": v(0, 0) * mm, "radius": 2.95 * mm});
            skCircle(sketch, "E11", {"center": v(0, 0) * mm, "radius": 10 * mm});
            skSolve(sketch);
        }
        {
            var Q0;
            Q0=makeQuery(id+"F3.imprint","IMPRINT",FACE,{"disambiguationData":[TD([[makeQuery(id+"F3.imprint","IMPRINT",EDGE,{"derivedFrom":sQuery(id+"F3.wireOp",EDGE,"E9")}),-1.0]])]});
            var Q1;
            Q1=makeQuery(id+"F3.imprint","IMPRINT",FACE,{"disambiguationData":[TD([[makeQuery(id+"F3.imprint","IMPRINT",EDGE,{"derivedFrom":sQuery(id+"F3.wireOp",EDGE,"E10")}),1.0]])]});
            extrude(context, id + "F4", {"entities" : qUnion([Q0, Q1]), "operationType" : NewBodyOperationType.REMOVE, "oppositeDirection" : true, "depth" : 9 * mm, "offsetDistance" : 25 * mm});
        }
    });
